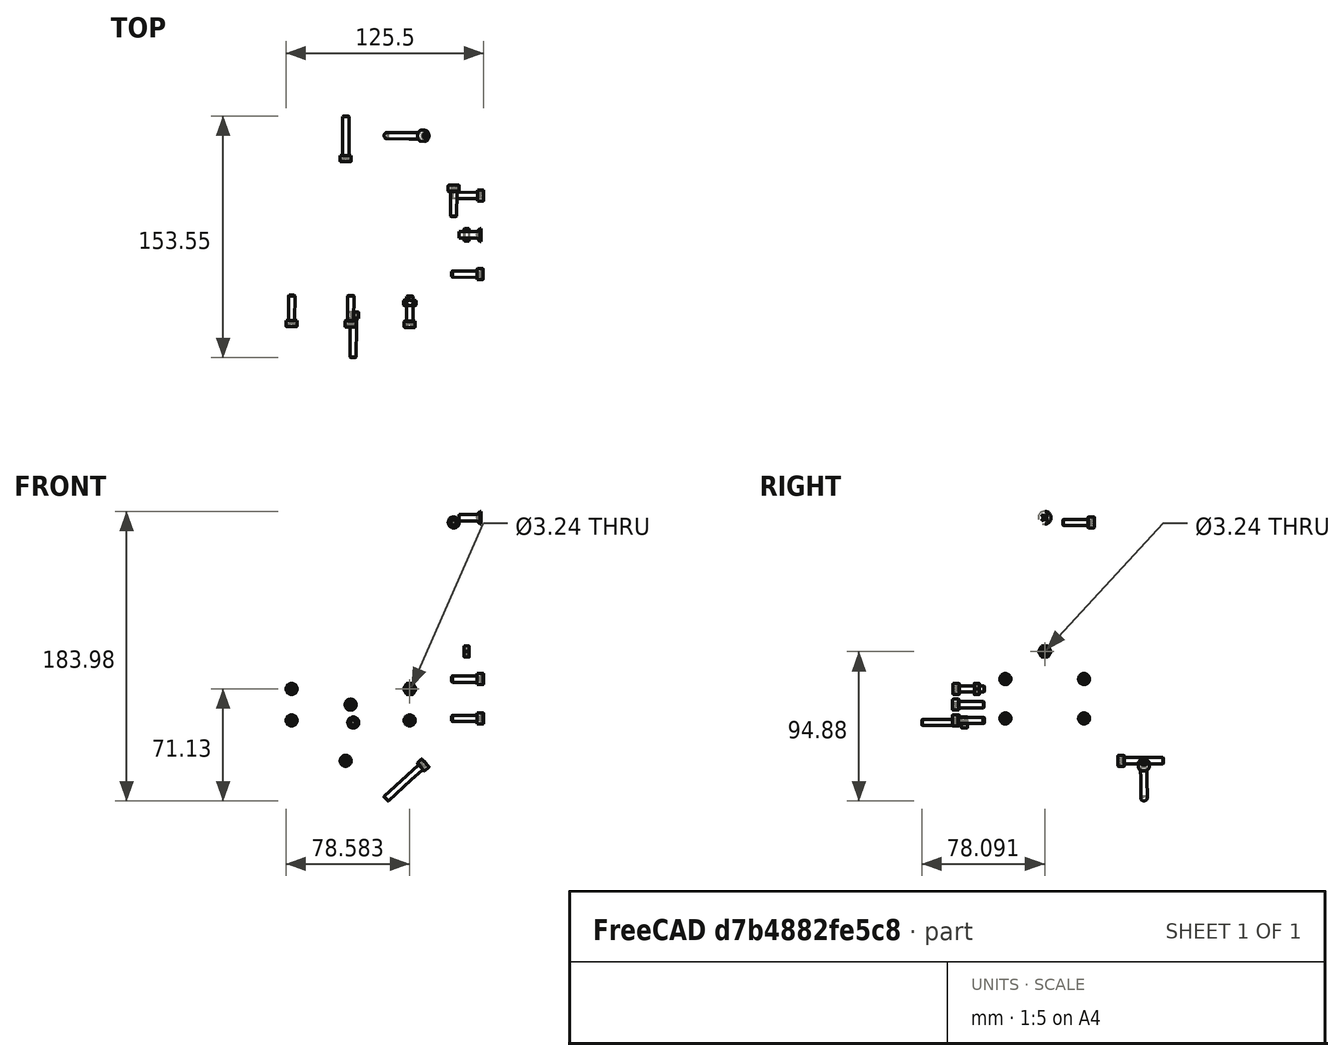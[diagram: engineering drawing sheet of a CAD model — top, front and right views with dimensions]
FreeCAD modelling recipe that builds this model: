
FCSTD DOCUMENT  (FreeCAD 1.1R42987 (Git))
Label: RobotAssembly
License: All rights reserved
LicenseURL: https://en.wikipedia.org/wiki/All_rights_reserved
objects: App::FeaturePython×68, App::Link×52, Part::FeaturePython×15, App::Point×3, Assembly::JointGroup×3, Assembly::AssemblyObject×3
note: 15 computed .brp shape members not serialized (recipe doc carries the construction recipe); baked Part::Feature solids carry a one-line shape summary decoded from their .brp
EXTERNAL_REF file=Body/Body.FCStd obj=Body
EXTERNAL_REF file=Imports/Neverest 20 Orbital.FCStd obj=am_3637_NeveRest_Orbital_20_Gearmotor_REV2
EXTERNAL_REF file=Body/Body.FCStd obj=Body001
EXTERNAL_REF file=Body/Body.FCStd obj=Body002
EXTERNAL_REF file=Imports/RaspberryPi3B+.FCStd obj=Ras_Pi_3B_
EXTERNAL_REF file=Body/Body.FCStd obj=Body003
EXTERNAL_REF file=Imports/MISUMI-Sar220.FCStd obj=Part__Feature001
EXTERNAL_REF file=Imports/V-Groove.FCStd obj=_609_0613_0004
EXTERNAL_REF file=Imports/V-Groove.FCStd obj=Body
EXTERNAL_REF file=Wheel/Wheel.FCStd obj=Body
EXTERNAL_REF file=Wheel/Wheel.FCStd obj=Body001
EXTERNAL_REF file=Slides Plate/SlidesPlate.FCStd obj=Body
EXTERNAL_REF file=Imports/MISUMI-Sar220.FCStd obj=Part__Feature
EXTERNAL_REF file=Variables.FCStd obj=Spreadsheet
EXTERNAL_REF file=Body/Body.FCStd obj=Body004
EXTERNAL_REF file=Body/Body.FCStd obj=Body007
EXTERNAL_REF file=Imports/Fan.FCStd obj=GUNCAIZHU_Ventilator_30x30x7_5_5V
EXTERNAL_REF file=Slides Motor Mount/SlidesMotorMount.FCStd obj=Body
EXTERNAL_REF file=Spool/Spool.FCStd obj=Body
EXTERNAL_REF file=Spool/Spool.FCStd obj=Body001
EXTERNAL_REF file=Passive Claw/PassiveClaw.FCStd obj=Part__Mirroring
EXTERNAL_REF file=Passive Claw/PassiveClaw.FCStd obj=Body
EXTERNAL_REF file=Body/Body.FCStd obj=Body008
EXTERNAL_REF file=Body/Body.FCStd obj=Body009

FEATURE [App::Point] Origin001
  Role = Origin
FEATURE [App::Link] Body
  LinkPlacement = pos=(-23.8017,-14.6889,-3.00006) rot=(0,0,-1;0.005858rad)
  LinkedObject = -> <external Body/Body.FCStd>#Body
  Placement = pos=(-23.8017,-14.6889,-3.00006) rot=(0,0,-1;0.005858rad)
FEATURE [App::Link] am_3637_NeveRest_Orbital_20_Gearmotor_REV2  label="am-3637 NeveRest Orbital 20 Gearmotor REV2"
  LinkPlacement = pos=(-23.0758,-34.8754,-19.558) rot=(0.999991,-0.002929,-0.002929;1.57081rad)
  LinkedObject = -> <external Imports/Neverest 20 Orbital.FCStd>#am_3637_NeveRest_Orbital_20_Gearmotor_REV2
  Placement = pos=(-23.0758,-34.8754,-19.558) rot=(0.999991,-0.002929,-0.002929;1.57081rad)
FEATURE [App::Link] Motor_Mount_Right  label="Motor Mount Right"
  LinkPlacement = pos=(-23.8017,-14.6889,-3.00006) rot=(0,0,-1;0.005858rad)
  LinkedObject = -> <external Body/Body.FCStd>#Body001
  Placement = pos=(-23.8017,-14.6889,-3.00006) rot=(0,0,-1;0.005858rad)
FEATURE [App::Link] Link  label="am-3637 NeveRest Orbital 20 Gearmotor REV003"
  LinkPlacement = pos=(-24.5276,5.49757,-19.558) rot=(0.002071,0.707105,0.707105;3.13745rad)
  LinkedObject = -> am_3637_NeveRest_Orbital_20_Gearmotor_REV2
  Placement = pos=(-24.5276,5.49757,-19.558) rot=(0.002071,0.707105,0.707105;3.13745rad)
FEATURE [App::Link] Slides_Mount  label="Slides Mount"
  LinkPlacement = pos=(-23.8017,-14.6889,-3.00006) rot=(0,0,-1;0.005858rad)
  LinkedObject = -> <external Body/Body.FCStd>#Body002
  Placement = pos=(-23.8017,-14.6889,-3.00006) rot=(0,0,-1;0.005858rad)
FEATURE [App::FeaturePython] Joint009  label="Fixed005"  # Assembly joint (typed FeaturePython)
  AngleMax = 0
  AngleMin = 0
  Detach1 = false
  Detach2 = false
  Distance = 0
  Distance2 = 0
  EnableAngleMax = false
  EnableAngleMin = false
  EnableLengthMax = false
  EnableLengthMin = false
  JointType = 0 (Fixed)
  LengthMax = 0
  LengthMin = 0
  Placement1 = pos=(75,25,30) rot=(0.57735,0.57735,0.57735;2.0944rad)
  Placement2 = pos=(75,25,30) rot=(0.57735,0.57735,0.57735;2.0944rad)
  Reference1 = -> Assembly [Slides_Mount.Edge32,Slides_Mount.Edge32]
  Reference2 = -> Assembly [Body.Edge44,Body.Edge44]
  Suppressed = false
FEATURE [Part::FeaturePython] Screw  label="M4x16-Screw124"  # WARN: FeaturePython — macro-defined, semantics opaque (R4)
  Diameter = 5
  Invert = false
  LeftHanded = false
  Length = 5
  LengthCustom = 16
  MatchOuter = false
  OffsetAngle = 0
  Placement = pos=(56.0505,-40.1572,26.9999) rot=(0.579605,0.576219,0.576219;2.09102rad)
  Thread = false
  Type = 74
FEATURE [App::FeaturePython] Joint012  label="Fixed007"  # Assembly joint (typed FeaturePython)
  AngleMax = 0
  AngleMin = 0
  Detach1 = false
  Detach2 = false
  Distance = 0
  Distance2 = 0
  EnableAngleMax = false
  EnableAngleMin = false
  EnableLengthMax = false
  EnableLengthMin = false
  JointType = 0 (Fixed)
  LengthMax = 0
  LengthMin = 0
  Placement2 = pos=(80,-25,30) rot=(0.57735,0.57735,0.57735;2.0944rad)
  Reference1 = -> Assembly [Screw.Edge26,Screw.Edge26]
  Reference2 = -> Assembly [Slides_Mount.Edge53,Slides_Mount.Edge53]
  Suppressed = false
FEATURE [Part::FeaturePython] Screw001  label="M4x16-Screw"  # WARN: FeaturePython — macro-defined, semantics opaque (R4)
  Diameter = 5
  Invert = false
  LeftHanded = false
  Length = 5
  LengthCustom = 16
  MatchOuter = false
  OffsetAngle = 0
  Placement = pos=(56.3434,9.84197,26.9999) rot=(0.579605,0.576219,0.576219;2.09102rad)
  Thread = false
  Type = 74
  expr: LengthCustom = <<M4x16-Screw124>>.LengthCustom
FEATURE [Part::FeaturePython] Screw002  label="M4x16-Screw125"  # WARN: FeaturePython — macro-defined, semantics opaque (R4)
  Diameter = 5
  Invert = false
  LeftHanded = false
  Length = 5
  LengthCustom = 16
  MatchOuter = false
  OffsetAngle = 0
  Placement = pos=(56.0505,-40.1572,1.99994) rot=(0.579605,0.576219,0.576219;2.09102rad)
  Thread = false
  Type = 74
  expr: LengthCustom = <<M4x16-Screw124>>.LengthCustom
FEATURE [Part::FeaturePython] Screw003  label="M4x16-Screw126"  # WARN: FeaturePython — macro-defined, semantics opaque (R4)
  Diameter = 5
  Invert = false
  LeftHanded = false
  Length = 5
  LengthCustom = 16
  MatchOuter = false
  OffsetAngle = 0
  Placement = pos=(56.3434,9.84197,1.99994) rot=(0.579605,0.576219,0.576219;2.09102rad)
  Thread = false
  Type = 74
  expr: LengthCustom = <<M4x16-Screw124>>.LengthCustom
FEATURE [App::FeaturePython] Joint013  label="Fixed008"  # Assembly joint (typed FeaturePython)
  AngleMax = 0
  AngleMin = 0
  Detach1 = false
  Detach2 = false
  Distance = 0
  Distance2 = 0
  EnableAngleMax = false
  EnableAngleMin = false
  EnableLengthMax = false
  EnableLengthMin = false
  JointType = 0 (Fixed)
  LengthMax = 0
  LengthMin = 0
  Placement2 = pos=(80,-25,5) rot=(0.57735,0.57735,0.57735;2.0944rad)
  Reference1 = -> Assembly [Screw002.Edge26,Screw002.Edge26]
  Reference2 = -> Assembly [Slides_Mount.Edge52,Slides_Mount.Edge52]
  Suppressed = false
FEATURE [App::FeaturePython] Joint014  label="Fixed009"  # Assembly joint (typed FeaturePython)
  AngleMax = 0
  AngleMin = 0
  Detach1 = false
  Detach2 = false
  Distance = 0
  Distance2 = 0
  EnableAngleMax = false
  EnableAngleMin = false
  EnableLengthMax = false
  EnableLengthMin = false
  JointType = 0 (Fixed)
  LengthMax = 0
  LengthMin = 0
  Placement2 = pos=(80,25,30) rot=(0.57735,0.57735,0.57735;2.0944rad)
  Reference1 = -> Assembly [Screw001.Edge26,Screw001.Edge26]
  Reference2 = -> Assembly [Slides_Mount.Edge51,Slides_Mount.Edge51]
  Suppressed = false
FEATURE [App::FeaturePython] Joint015  label="Fixed010"  # Assembly joint (typed FeaturePython)
  AngleMax = 0
  AngleMin = 0
  Detach1 = false
  Detach2 = false
  Distance = 0
  Distance2 = 0
  EnableAngleMax = false
  EnableAngleMin = false
  EnableLengthMax = false
  EnableLengthMin = false
  JointType = 0 (Fixed)
  LengthMax = 0
  LengthMin = 0
  Placement2 = pos=(80,25,5) rot=(0.57735,0.57735,0.57735;2.0944rad)
  Reference1 = -> Assembly [Screw003.Edge26,Screw003.Edge26]
  Reference2 = -> Assembly [Slides_Mount.Edge50,Slides_Mount.Edge50]
  Suppressed = false
FEATURE [Part::FeaturePython] Screw004  label="M4x16-Screw127"  # WARN: FeaturePython — macro-defined, semantics opaque (R4)
  Diameter = 5
  Invert = false
  LeftHanded = false
  Length = 5
  LengthCustom = 16
  MatchOuter = false
  OffsetAngle = 0
  Placement = pos=(-61.6233,-69.4683,20.7499) rot=(0.999991,-0.002929,-0.002929;1.57081rad)
  Thread = false
  Type = 74
  expr: LengthCustom = <<M4x16-Screw124>>.LengthCustom
FEATURE [Part::FeaturePython] Screw005  label="M4x16-Screw128"  # WARN: FeaturePython — macro-defined, semantics opaque (R4)
  Diameter = 5
  Invert = false
  LeftHanded = false
  Length = 5
  LengthCustom = 16
  MatchOuter = false
  OffsetAngle = 0
  Placement = pos=(-61.6233,-69.4683,0.749943) rot=(0.999991,-0.002929,-0.002929;1.57081rad)
  Thread = false
  Type = 74
  expr: LengthCustom = <<M4x16-Screw127>>.LengthCustom
FEATURE [Part::FeaturePython] Screw006  label="M4x16-Screw129"  # WARN: FeaturePython — macro-defined, semantics opaque (R4)
  Diameter = 5
  Invert = false
  LeftHanded = false
  Length = 5
  LengthCustom = 16
  MatchOuter = false
  OffsetAngle = 0
  Placement = pos=(-24.1239,-69.688,10.7499) rot=(0.999991,-0.002929,-0.002929;1.57081rad)
  Thread = false
  Type = 74
  expr: LengthCustom = <<M4x16-Screw127>>.LengthCustom
FEATURE [Part::FeaturePython] Screw007  label="M4x16-Screw130"  # WARN: FeaturePython — macro-defined, semantics opaque (R4)
  Diameter = 5
  Invert = false
  LeftHanded = false
  Length = 5
  LengthCustom = 16
  MatchOuter = false
  OffsetAngle = 0
  Placement = pos=(13.3754,-69.9077,0.749943) rot=(0.999991,-0.002929,-0.002929;1.57081rad)
  Thread = false
  Type = 74
  expr: LengthCustom = <<M4x16-Screw127>>.LengthCustom
FEATURE [App::Link] Link001  label="M4x16-Screw026"
  LinkPlacement = pos=(13.3754,-69.9077,20.7499) rot=(0.999991,-0.002929,-0.002929;1.57081rad)
  LinkedObject = -> Screw007
  Placement = pos=(13.3754,-69.9077,20.7499) rot=(0.999991,-0.002929,-0.002929;1.57081rad)
FEATURE [App::Link] Ras_Pi_3B_179  label="Ras Pi 3B+179"
  LinkPlacement = pos=(-12.1701,7.74332,-5.72205e-05) rot=(0.002071,0.707105,0.707105;3.13745rad)
  LinkedObject = -> <external Imports/RaspberryPi3B+.FCStd>#Ras_Pi_3B_
  Placement = pos=(-12.1701,7.74332,-5.72205e-05) rot=(0.002071,0.707105,0.707105;3.13745rad)
FEATURE [Part::FeaturePython] Screw008  label="M4x14-Screw"  # WARN: FeaturePython — macro-defined, semantics opaque (R4)
  Diameter = 6
  Invert = false
  LeftHanded = false
  Length = 4
  LengthCustom = 14
  MatchOuter = false
  OffsetAngle = 0
  Placement = pos=(58.7504,-15.1726,129.5) rot=(0.002929,0.999991,-0.002929;1.57081rad)
  Thread = false
  Type = 77
FEATURE [App::Link] Link002  label="M4x14-Screw001"
  LinkPlacement = pos=(58.7504,-15.1726,44.4999) rot=(0.002929,0.999991,-0.002929;1.57081rad)
  LinkedObject = -> Screw008
  Placement = pos=(58.7504,-15.1726,44.4999) rot=(0.002929,0.999991,-0.002929;1.57081rad)
FEATURE [Part::FeaturePython] Nut  label="M4-Nut"  # WARN: FeaturePython — macro-defined, semantics opaque (R4)
  Diameter = 6
  Invert = false
  LeftHanded = false
  MatchOuter = false
  OffsetAngle = 0
  Placement = pos=(47.9971,-15.1096,44.4999) rot=(0.579605,0.576219,0.576219;2.09102rad)
  Thread = false
  Type = 31
FEATURE [App::FeaturePython] Joint023  label="Fixed017"  # Assembly joint (typed FeaturePython)
  AngleMax = 0
  AngleMin = 0
  Detach1 = false
  Detach2 = false
  Distance = 0
  Distance2 = 0
  EnableAngleMax = false
  EnableAngleMin = false
  EnableLengthMax = false
  EnableLengthMin = false
  JointType = 0 (Fixed)
  LengthMax = 0
  LengthMin = 0
  Placement1 = pos=(0,0,3.2) rot=(0,0,1;0rad)
  Placement2 = pos=(75,-5.86e-14,47.5) rot=(0.57735,0.57735,0.57735;2.0944rad)
  Reference1 = -> Assembly [Nut.Edge2,Nut.Edge2]
  Reference2 = -> Assembly [Slides_Mount.Edge34,Slides_Mount.Edge34]
  Suppressed = false
FEATURE [App::FeaturePython] Joint027  label="Fixed021"  # Assembly joint (typed FeaturePython)
  AngleMax = 0
  AngleMin = 0
  Detach1 = false
  Detach2 = false
  Distance = 0
  Distance2 = 0
  EnableAngleMax = false
  EnableAngleMin = false
  EnableLengthMax = false
  EnableLengthMin = false
  JointType = 0 (Fixed)
  LengthMax = 0
  LengthMin = 0
  Offset2 = pos=(0,0,0) rot=(0,0,1;1.5708rad)
  Placement1 = pos=(-50,-30,3) rot=(0,0,1;0rad)
  Placement2 = pos=(61.5,0,-52.5) rot=(0,0.707107,0.707107;3.14159rad)
  Reference1 = -> Assembly [Body.Edge214,Body.Edge214]
  Reference2 = -> Assembly [Ras_Pi_3B_179.Part__Feature014.Edge10,Ras_Pi_3B_179.Part__Feature014.Edge10]
  Suppressed = false
FEATURE [App::Link] Body_Top  label="Body Top"
  LinkPlacement = pos=(-23.8017,-14.6889,-3.00006) rot=(0,0,-1;0.005858rad)
  LinkedObject = -> <external Body/Body.FCStd>#Body003
  Placement = pos=(-23.8017,-14.6889,-3.00006) rot=(0,0,-1;0.005858rad)
FEATURE [App::FeaturePython] Joint028  label="Fixed022"  # Assembly joint (typed FeaturePython)
  AngleMax = 0
  AngleMin = 0
  Detach1 = false
  Detach2 = false
  Distance = 0
  Distance2 = 0
  EnableAngleMax = false
  EnableAngleMin = false
  EnableLengthMax = false
  EnableLengthMin = false
  JointType = 0 (Fixed)
  LengthMax = 0
  LengthMin = 0
  Placement1 = pos=(-66,-41,35) rot=(0,0,1;0rad)
  Placement2 = pos=(-66,-41,35) rot=(0,0,1;0rad)
  Reference1 = -> Assembly [Body.Edge21,Body.Edge21]
  Reference2 = -> Assembly [Body_Top.Edge98,Body_Top.Edge98]
  Suppressed = false
FEATURE [Part::FeaturePython] Nut001  label="M4-Nut014"  # WARN: FeaturePython — macro-defined, semantics opaque (R4)
  Diameter = 6
  Invert = false
  LeftHanded = false
  MatchOuter = false
  OffsetAngle = 0
  Placement = pos=(13.4528,-56.7079,20.7499) rot=(0.999991,-0.002929,-0.002929;1.57081rad)
  Thread = false
  Type = 31
FEATURE [App::FeaturePython] Joint029  label="Fixed023"  # Assembly joint (typed FeaturePython)
  AngleMax = 0
  AngleMin = 0
  Detach1 = false
  Detach2 = false
  Distance = 0
  Distance2 = 0
  EnableAngleMax = false
  EnableAngleMin = false
  EnableLengthMax = false
  EnableLengthMin = false
  JointType = 0 (Fixed)
  LengthMax = 0
  LengthMin = 0
  Placement1 = pos=(0,-3.6e-15,3.2) rot=(0,0,1;0rad)
  Placement2 = pos=(37.5,-45,23.75) rot=(1,0,0;1.5708rad)
  Reference1 = -> Assembly [Nut001.Edge2,Nut001.Edge2]
  Reference2 = -> Assembly [Body.Edge89,Body.Edge89]
  Suppressed = false
FEATURE [App::Link] Link004  label="M4-Nut003"
  LinkPlacement = pos=(-23.5193,33.5103,10.7499) rot=(0.999991,-0.002929,-0.002929;1.57081rad)
  LinkedObject = -> Nut001
  Placement = pos=(-23.5193,33.5103,10.7499) rot=(0.999991,-0.002929,-0.002929;1.57081rad)
FEATURE [App::Link] Link005  label="M4-Nut004"
  LinkPlacement = pos=(-61.0562,27.3301,0.749943) rot=(0.999991,-0.002929,0.002929;4.71238rad)
  LinkedObject = -> Link004
  Placement = pos=(-61.0562,27.3301,0.749943) rot=(0.999991,-0.002929,0.002929;4.71238rad)
FEATURE [App::Link] Link007  label="M4-Nut006"
  LinkPlacement = pos=(-61.5459,-56.2685,20.7499) rot=(0.999991,-0.002929,-0.002929;1.57081rad)
  LinkedObject = -> Nut
  Placement = pos=(-61.5459,-56.2685,20.7499) rot=(0.999991,-0.002929,-0.002929;1.57081rad)
FEATURE [App::Link] Link008  label="M4-Nut007"
  LinkPlacement = pos=(13.9613,30.0906,0.749943) rot=(-0.002071,-0.707105,0.707105;3.13745rad)
  LinkedObject = -> Link007
  Placement = pos=(13.9613,30.0906,0.749943) rot=(-0.002071,-0.707105,0.707105;3.13745rad)
FEATURE [App::Link] Link009  label="M4-Nut008"
  LinkPlacement = pos=(-61.0562,27.3301,20.7499) rot=(0.999991,-0.002929,0.002929;4.71238rad)
  LinkedObject = -> Link008
  Placement = pos=(-61.0562,27.3301,20.7499) rot=(0.999991,-0.002929,0.002929;4.71238rad)
FEATURE [App::Link] Link010  label="M4-Nut009"
  LinkPlacement = pos=(42.8507,-40.0798,26.9999) rot=(0.579605,0.576219,0.576219;2.09102rad)
  LinkedObject = -> Link009
  Placement = pos=(42.8507,-40.0798,26.9999) rot=(0.579605,0.576219,0.576219;2.09102rad)
FEATURE [App::FeaturePython] Joint031  label="Fixed025"  # Assembly joint (typed FeaturePython)
  AngleMax = 0
  AngleMin = 0
  Detach1 = false
  Detach2 = false
  Distance = 0
  Distance2 = 0
  EnableAngleMax = false
  EnableAngleMin = false
  EnableLengthMax = false
  EnableLengthMin = false
  JointType = 0 (Fixed)
  LengthMax = 0
  LengthMin = 0
  Placement1 = pos=(0,-3.6e-15,3.2) rot=(0,0,1;0rad)
  Placement2 = pos=(-37.5,-45,23.75) rot=(1,0,0;1.5708rad)
  Reference1 = -> Assembly [Link007.Edge2,Link007.Edge2]
  Reference2 = -> Assembly [Body.Edge88,Body.Edge88]
  Suppressed = false
FEATURE [App::FeaturePython] Joint034  label="Fixed028"  # Assembly joint (typed FeaturePython)
  AngleMax = 0
  AngleMin = 0
  Detach1 = false
  Detach2 = false
  Distance = 0
  Distance2 = 0
  EnableAngleMax = false
  EnableAngleMin = false
  EnableLengthMax = false
  EnableLengthMin = false
  JointType = 0 (Fixed)
  LengthMax = 0
  LengthMin = 0
  Placement1 = pos=(7.1e-15,0,3.2) rot=(0,0,1;0rad)
  Placement2 = pos=(-37.5,45,23.75) rot=(1,0,0;1.5708rad)
  Reference1 = -> Assembly [Link009.Edge2,Link009.Edge2]
  Reference2 = -> Assembly [Body.Edge122,Body.Edge122]
  Suppressed = false
FEATURE [App::Link] Link011  label="M4-Nut010"
  LinkPlacement = pos=(13.9425,26.8907,20.7499) rot=(0.999991,-0.002929,0.002929;4.71238rad)
  LinkedObject = -> Link009
  Placement = pos=(13.9425,26.8907,20.7499) rot=(0.999991,-0.002929,0.002929;4.71238rad)
FEATURE [App::Link] Link012  label="M4-Nut011"
  LinkPlacement = pos=(43.1436,9.9193,1.99994) rot=(0.579605,0.576219,0.576219;2.09102rad)
  LinkedObject = -> Link008
  Placement = pos=(43.1436,9.9193,1.99994) rot=(0.579605,0.576219,0.576219;2.09102rad)
FEATURE [App::Link] Link013  label="M4-Nut012"
  LinkPlacement = pos=(43.1436,9.9193,26.9999) rot=(0.579605,0.576219,0.576219;2.09102rad)
  LinkedObject = -> Link010
  Placement = pos=(43.1436,9.9193,26.9999) rot=(0.579605,0.576219,0.576219;2.09102rad)
FEATURE [App::FeaturePython] Joint037  label="Fixed031"  # Assembly joint (typed FeaturePython)
  AngleMax = 0
  AngleMin = 0
  Detach1 = false
  Detach2 = false
  Distance = 0
  Distance2 = 0
  EnableAngleMax = false
  EnableAngleMin = false
  EnableLengthMax = false
  EnableLengthMin = false
  JointType = 0 (Fixed)
  LengthMax = 0
  LengthMin = 0
  Placement1 = pos=(0,0,3.2) rot=(0,0,1;0rad)
  Placement2 = pos=(37.5,45,23.75) rot=(1,0,0;1.5708rad)
  Reference1 = -> Assembly [Link011.Edge2,Link011.Edge2]
  Reference2 = -> Assembly [Body.Edge121,Body.Edge121]
  Suppressed = false
FEATURE [App::Link] Link014  label="M4x16-Screw034"
  LinkPlacement = pos=(-23.4795,40.3101,10.7499) rot=(0.002071,0.707105,0.707105;3.13745rad)
  LinkedObject = -> Screw004
  Placement = pos=(-23.4795,40.3101,10.7499) rot=(0.002071,0.707105,0.707105;3.13745rad)
FEATURE [App::Link] Link015  label="M4x16-Screw035"
  LinkPlacement = pos=(-60.9788,40.5298,20.7499) rot=(0.002071,0.707105,0.707105;3.13745rad)
  LinkedObject = -> Link014
  Placement = pos=(-60.9788,40.5298,20.7499) rot=(0.002071,0.707105,0.707105;3.13745rad)
FEATURE [App::Link] Link016  label="M4x16-Screw036"
  LinkPlacement = pos=(14.0199,40.0904,0.749943) rot=(0.002071,0.707105,0.707105;3.13745rad)
  LinkedObject = -> Link015
  Placement = pos=(14.0199,40.0904,0.749943) rot=(0.002071,0.707105,0.707105;3.13745rad)
FEATURE [App::Link] Link017  label="M4x16-Screw037"
  LinkPlacement = pos=(-60.9788,40.5298,0.749943) rot=(0.002071,0.707105,0.707105;3.13745rad)
  LinkedObject = -> Link016
  Placement = pos=(-60.9788,40.5298,0.749943) rot=(0.002071,0.707105,0.707105;3.13745rad)
FEATURE [App::Link] Link018  label="M4x16-Screw038"
  LinkPlacement = pos=(14.0199,40.0904,20.7499) rot=(0.002071,0.707105,0.707105;3.13745rad)
  LinkedObject = -> Link017
  Placement = pos=(14.0199,40.0904,20.7499) rot=(0.002071,0.707105,0.707105;3.13745rad)
FEATURE [App::FeaturePython] GroundedJoint  # Assembly grounded joint (typed FeaturePython)
  ObjectToGround = -> Body
FEATURE [App::Link] SAR2_20_b  label="SAR2-20_b"
  LinkPlacement = pos=(63.5382,-25.2008,-55.5001) rot=(0,0,-1;0.005858rad)
  LinkedObject = -> <external Imports/MISUMI-Sar220.FCStd>#Part__Feature001
  Placement = pos=(63.5382,-25.2008,-55.5001) rot=(0,0,-1;0.005858rad)
FEATURE [App::FeaturePython] Joint045  label="Fixed038"  # Assembly joint (typed FeaturePython)
  AngleMax = 0
  AngleMin = 0
  Detach1 = false
  Detach2 = false
  Distance = 0
  Distance2 = 0
  EnableAngleMax = false
  EnableAngleMin = false
  EnableLengthMax = false
  EnableLengthMin = false
  JointType = 0 (Fixed)
  LengthMax = 0
  LengthMin = 0
  Offset2 = pos=(0,0,0) rot=(0,0,-1;1.5708rad)
  Placement1 = pos=(-7.4,10,185) rot=(0,1,0;1.5708rad)
  Placement2 = pos=(80,-5.68e-14,132.5) rot=(0,1,0;1.5708rad)
  Reference1 = -> Assembly [SAR2_20_b.Edge129,SAR2_20_b.Edge129]
  Reference2 = -> Assembly [Slides_Mount.Edge48,Slides_Mount.Edge48]
  Suppressed = false
FEATURE [App::FeaturePython] Joint046  label="Fixed039"  # Assembly joint (typed FeaturePython)
  AngleMax = 0
  AngleMin = 0
  Detach1 = false
  Detach2 = false
  Distance = 0
  Distance2 = 0
  EnableAngleMax = false
  EnableAngleMin = false
  EnableLengthMax = false
  EnableLengthMin = false
  JointType = 0 (Fixed)
  LengthMax = 0
  LengthMin = 0
  Placement1 = pos=(0,1.8e-15,-2.55355) rot=(0,0,1;0rad)
  Placement2 = pos=(-7.4,10,185) rot=(0,1,0;1.5708rad)
  Reference1 = -> Assembly [Screw008.Edge4,Screw008.Edge4]
  Reference2 = -> Assembly [SAR2_20_b.Edge129,SAR2_20_b.Edge129]
  Suppressed = false
FEATURE [App::FeaturePython] Joint047  label="Fixed040"  # Assembly joint (typed FeaturePython)
  AngleMax = 0
  AngleMin = 0
  Detach1 = false
  Detach2 = false
  Distance = 0
  Distance2 = 0
  EnableAngleMax = false
  EnableAngleMin = false
  EnableLengthMax = false
  EnableLengthMin = false
  JointType = 0 (Fixed)
  LengthMax = 0
  LengthMin = 0
  Placement1 = pos=(0,1.8e-15,-2.55355) rot=(0,0,1;0rad)
  Placement2 = pos=(-7.4,10,100) rot=(0,1,0;1.5708rad)
  Reference1 = -> Assembly [Link002.Edge4,Link002.Edge4]
  Reference2 = -> Assembly [SAR2_20_b.Edge130,SAR2_20_b.Edge130]
  Suppressed = false
FEATURE [App::Link] _609_0613_0007  label="1609-0613-0007"
  LinkPlacement = pos=(41.3026,2.92997,126.5) rot=(0.002929,0.999991,-0.002929;1.57081rad)
  LinkedObject = -> <external Imports/V-Groove.FCStd>#_609_0613_0004
  Placement = pos=(41.3026,2.92997,126.5) rot=(0.002929,0.999991,-0.002929;1.57081rad)
FEATURE [App::Link] StringGuard
  LinkPlacement = pos=(41.3041,3.17997,126.5) rot=(0,0,-1;0.005858rad)
  LinkedObject = -> <external Imports/V-Groove.FCStd>#Body
  Placement = pos=(41.3041,3.17997,126.5) rot=(0,0,-1;0.005858rad)
FEATURE [Part::FeaturePython] Screw009  label="M4x16-Screw131"  # WARN: FeaturePython — macro-defined, semantics opaque (R4)
  Diameter = 5
  Invert = false
  LeftHanded = false
  Length = 11
  LengthCustom = 16
  MatchOuter = false
  OffsetAngle = 0
  Placement = pos=(41.3583,12.4298,126.5) rot=(0.999991,-0.002929,0.002929;4.71238rad)
  Thread = false
  Type = 74
  expr: LengthCustom = <<M4x16-Screw124>>.LengthCustom
FEATURE [App::FeaturePython] Joint053  label="Fixed045"  # Assembly joint (typed FeaturePython)
  AngleMax = 0
  AngleMin = 0
  Detach1 = false
  Detach2 = false
  Distance = 0
  Distance2 = 0
  EnableAngleMax = false
  EnableAngleMin = false
  EnableLengthMax = false
  EnableLengthMin = false
  JointType = 0 (Fixed)
  LengthMax = 0
  LengthMin = 0
  Offset2 = pos=(0,0,0) rot=(0,0,1;3.14159rad)
  Placement1 = pos=(-7.1e-15,-3.25,0) rot=(1,0,0;1.5708rad)
  Placement2 = pos=(65,15,129.5) rot=(1,0,0;4.71239rad)
  Reference1 = -> Assembly [StringGuard.Edge9,StringGuard.Edge9]
  Reference2 = -> Assembly [Slides_Mount.Edge58,Slides_Mount.Edge58]
  Suppressed = false
FEATURE [App::FeaturePython] Joint054  label="Fixed046"  # Assembly joint (typed FeaturePython)
  AngleMax = 0
  AngleMin = 0
  Detach1 = false
  Detach2 = false
  Distance = 0
  Distance2 = 0
  EnableAngleMax = false
  EnableAngleMin = false
  EnableLengthMax = false
  EnableLengthMin = false
  JointType = 0 (Fixed)
  LengthMax = 0
  LengthMin = 0
  Placement1 = pos=(-7.1e-15,9.25,0) rot=(1,0,0;1.5708rad)
  Reference1 = -> Assembly [StringGuard.Edge35,StringGuard.Edge35]
  Reference2 = -> Assembly [Screw009.Edge26,Screw009.Edge26]
  Suppressed = false
FEATURE [App::FeaturePython] Joint055  label="Revolute047"  # Assembly joint (typed FeaturePython)
  AngleMax = 0
  AngleMin = 0
  Detach1 = false
  Detach2 = false
  Distance = 0
  Distance2 = 0
  EnableAngleMax = false
  EnableAngleMin = false
  EnableLengthMax = false
  EnableLengthMin = false
  JointType = 1 (Revolute)
  LengthMax = 0
  LengthMin = 0
  Placement1 = pos=(0,0,0) rot=(0.57735,-0.57735,0.57735;2.0944rad)
  Placement2 = pos=(-7.1e-15,-0.25,0) rot=(1,0,0;1.5708rad)
  Reference1 = -> Assembly [_609_0613_0007.Part__Feature002.Edge108,_609_0613_0007.Part__Feature002.Edge108]
  Reference2 = -> Assembly [StringGuard.Edge2,StringGuard.Edge2]
  Suppressed = false
FEATURE [App::Link] Link020  label="Motor Mount Right001"
  LinkPlacement = pos=(-23.8017,-14.6889,-3.00006) rot=(0,0,1;3.13573rad)
  LinkedObject = -> Motor_Mount_Right
  Placement = pos=(-23.8017,-14.6889,-3.00006) rot=(0,0,1;3.13573rad)
FEATURE [App::FeaturePython] Joint056  label="Fixed048"  # Assembly joint (typed FeaturePython)
  AngleMax = 0
  AngleMin = 0
  Detach1 = false
  Detach2 = false
  Distance = 0
  Distance2 = 0
  EnableAngleMax = false
  EnableAngleMin = false
  EnableLengthMax = false
  EnableLengthMin = false
  JointType = 0 (Fixed)
  LengthMax = 0
  LengthMin = 0
  Placement1 = pos=(-28,-50,-29) rot=(1,0,0;1.5708rad)
  Placement2 = pos=(0,0,32.1564) rot=(0,0,1;0rad)
  Reference1 = -> Assembly [Link020.Edge28,Link020.Edge28]
  Reference2 = -> Assembly [Link.Part__Feature.Edge165,Link.Part__Feature.Edge165]
  Suppressed = false
FEATURE [App::Link] Wheel
  LinkPlacement = pos=(4.66789,64.8507,-31.9659) rot=(-0.29634,0.676219,-0.674471;3.72505rad)
  LinkedObject = -> <external Wheel/Wheel.FCStd>#Body
  Placement = pos=(4.66789,64.8507,-31.9659) rot=(-0.29634,0.676219,-0.674471;3.72505rad)
FEATURE [App::Link] Clamp
  LinkPlacement = pos=(4.66789,64.8507,-31.9659) rot=(-0.29634,0.676219,-0.674471;3.72505rad)
  LinkedObject = -> <external Wheel/Wheel.FCStd>#Body001
  Placement = pos=(4.66789,64.8507,-31.9659) rot=(-0.29634,0.676219,-0.674471;3.72505rad)
FEATURE [App::Link] Link021  label="Clamp001"
  LinkPlacement = pos=(-52.0438,-60.2292,-31.9979) rot=(-0.543151,0.595306,-0.592114;4.1421rad)
  LinkedObject = -> Clamp
  Placement = pos=(-52.0438,-60.2292,-31.9979) rot=(-0.543151,0.595306,-0.592114;4.1421rad)
FEATURE [App::Link] Link022  label="Wheel001"
  LinkPlacement = pos=(-52.241,-94.2287,-32.021) rot=(-0.60929,0.562485,0.558906;2.04236rad)
  LinkedObject = -> Wheel
  Placement = pos=(-52.241,-94.2287,-32.021) rot=(-0.60929,0.562485,0.558906;2.04236rad)
FEATURE [App::Link] Slides_Plate  label="Slides Plate"
  LinkPlacement = pos=(69.1967,-15.2338,-40.5001) rot=(-0.575095,0.578474,0.578474;4.18541rad)
  LinkedObject = -> <external Slides Plate/SlidesPlate.FCStd>#Body
  Placement = pos=(69.1967,-15.2338,-40.5001) rot=(-0.575095,0.578474,0.578474;4.18541rad)
FEATURE [App::Link] SAR2_20_r  label="SAR2-20_r"
  LinkPlacement = pos=(58.3615,-21.2204,-55.5001) rot=(0,0,-1;0.005858rad)
  LinkedObject = -> <external Imports/MISUMI-Sar220.FCStd>#Part__Feature
  Placement = pos=(58.3615,-21.2204,-55.5001) rot=(0,0,-1;0.005858rad)
FEATURE [App::FeaturePython] Joint081  label="Slider"  # Assembly joint (typed FeaturePython)
  AngleMax = 0
  AngleMin = 0
  Detach1 = false
  Detach2 = false
  Distance = 0
  Distance2 = 0
  EnableAngleMax = false
  EnableAngleMin = false
  EnableLengthMax = true
  EnableLengthMin = true
  JointType = 3 (Slider)
  LengthMax = 120
  LengthMin = 0
  Offset1 = pos=(2.9952,0,0) rot=(0,0,1;0rad)
  Placement1 = pos=(-1.90256,10,200) rot=(0,0,1;0rad)
  Placement2 = pos=(3.29741,6.05,200) rot=(0,0,1;0rad)
  Reference1 = -> Assembly [SAR2_20_b.Face57,SAR2_20_b.Face57]
  Reference2 = -> Assembly [SAR2_20_r.Face24,SAR2_20_r.Face24]
  Suppressed = false
FEATURE [App::FeaturePython] Joint082  label="Fixed059"  # Assembly joint (typed FeaturePython)
  AngleMax = 0
  AngleMin = 0
  Detach1 = false
  Detach2 = false
  Distance = 0
  Distance2 = 0
  EnableAngleMax = false
  EnableAngleMin = false
  EnableLengthMax = false
  EnableLengthMin = false
  JointType = 0 (Fixed)
  LengthMax = 0
  LengthMin = 0
  Offset2 = pos=(0,0,0) rot=(0,0,-1;1.5708rad)
  Placement1 = pos=(1.8e-15,7.82e-14,5) rot=(0,0,1;0rad)
  Placement2 = pos=(5.8,6.05,15) rot=(-0.57735,0.57735,-0.57735;2.0944rad)
  Reference1 = -> Assembly [Slides_Plate.Edge58,Slides_Plate.Edge58]
  Reference2 = -> Assembly [SAR2_20_r.Edge60,SAR2_20_r.Edge60]
  Suppressed = false
FEATURE [App::Point] Origin003
  Role = Origin
FEATURE [Assembly::JointGroup] Joints001
FEATURE [Assembly::AssemblyObject] Assembly001
  Group = -> [Joints001]
  Origin = -> Origin002
  Type = Assembly
FEATURE [App::FeaturePython] Joint083  label="Revolute065"  # Assembly joint (typed FeaturePython)
  AngleMax = 0
  AngleMin = 0
  Detach1 = false
  Detach2 = false
  Distance = 0
  Distance2 = 0
  EnableAngleMax = false
  EnableAngleMin = false
  EnableLengthMax = false
  EnableLengthMin = false
  JointType = 1 (Revolute)
  LengthMax = 0
  LengthMin = 0
  Offset2 = pos=(0,0,5) rot=(0,0,1;0rad)
  Placement1 = pos=(-0.0231521,0.025307,21.5) rot=(0,0,1;0rad)
  Placement2 = pos=(0,0,40.3614) rot=(0,0,1;0rad)
  Reference1 = -> Assembly [Wheel.Edge52,Wheel.Edge52]
  Reference2 = -> Assembly [Link.Part__Feature.Edge15,Link.Part__Feature.Edge15]
  Suppressed = false
FEATURE [App::FeaturePython] Joint084  label="Fixed061"  # Assembly joint (typed FeaturePython)
  AngleMax = 0
  AngleMin = 0
  Detach1 = false
  Detach2 = false
  Distance = 0
  Distance2 = 0
  EnableAngleMax = false
  EnableAngleMin = false
  EnableLengthMax = false
  EnableLengthMin = false
  JointType = 0 (Fixed)
  LengthMax = 0
  LengthMin = 0
  Offset2 = pos=(0,0,1.5) rot=(0,0,1;0rad)
  Placement1 = pos=(-8.46528,0.75,17) rot=(0,0.707107,0.707107;3.14159rad)
  Placement2 = pos=(-8.46528,0.75,17) rot=(0,0.707107,0.707107;3.14159rad)
  Reference1 = -> Assembly [Clamp.Edge30,Clamp.Edge30]
  Reference2 = -> Assembly [Wheel.Edge31,Wheel.Edge31]
  Suppressed = false
  expr: .Offset2.Base.z = Variables#Spreadsheet.WheelClampToShaftDist
FEATURE [App::FeaturePython] Joint085  label="Revolute064"  # Assembly joint (typed FeaturePython)
  AngleMax = 0
  AngleMin = 0
  Detach1 = false
  Detach2 = false
  Distance = 0
  Distance2 = 0
  EnableAngleMax = false
  EnableAngleMin = false
  EnableLengthMax = false
  EnableLengthMin = false
  JointType = 1 (Revolute)
  LengthMax = 0
  LengthMin = 0
  Offset2 = pos=(0,0,5) rot=(0,0,1;0rad)
  Placement1 = pos=(-0.0231521,0.025307,21.5) rot=(0,0,1;0rad)
  Placement2 = pos=(0,0,40.3614) rot=(0,0,1;0rad)
  Reference1 = -> Assembly [Link022.Edge52,Link022.Edge52]
  Reference2 = -> Assembly [am_3637_NeveRest_Orbital_20_Gearmotor_REV2.Part__Feature.Edge15,am_3637_NeveRest_Orbital_20_Gearmotor_REV2.Part__Feature.Edge15]
  Suppressed = false
  expr: .Offset2.Base.z = <<Revolute065>>.Offset2.Base.z
FEATURE [App::FeaturePython] Joint086  label="Fixed063"  # Assembly joint (typed FeaturePython)
  AngleMax = 0
  AngleMin = 0
  Detach1 = false
  Detach2 = false
  Distance = 0
  Distance2 = 0
  EnableAngleMax = false
  EnableAngleMin = false
  EnableLengthMax = false
  EnableLengthMin = false
  JointType = 0 (Fixed)
  LengthMax = 0
  LengthMin = 0
  Offset2 = pos=(0,0,1.5) rot=(0,0,1;3.14159rad)
  Placement1 = pos=(-8.46528,0.75,17) rot=(0,0.707107,0.707107;3.14159rad)
  Placement2 = pos=(8.44212,0.75,17) rot=(-1,0,0;1.5708rad)
  Reference1 = -> Assembly [Link021.Edge30,Link021.Edge30]
  Reference2 = -> Assembly [Link022.Edge36,Link022.Edge36]
  Suppressed = false
  expr: .Offset2.Base.z = Variables#Spreadsheet.WheelClampToShaftDist
FEATURE [Part::FeaturePython] Screw010  label="M4x30-Screw"  # WARN: FeaturePython — macro-defined, semantics opaque (R4)
  Diameter = 5
  Invert = false
  LeftHanded = false
  Length = 8
  LengthCustom = 30
  MatchOuter = false
  OffsetAngle = 0
  Placement = pos=(20.4333,47.758,-28.9634) rot=(0.404062,-0.001184,0.914731;3.13623rad)
  Thread = false
  Type = 74
FEATURE [App::FeaturePython] Joint087  label="Fixed064"  # Assembly joint (typed FeaturePython)
  AngleMax = 0
  AngleMin = 0
  Detach1 = false
  Detach2 = false
  Distance = 0
  Distance2 = 0
  EnableAngleMax = false
  EnableAngleMin = false
  EnableLengthMax = false
  EnableLengthMin = false
  JointType = 0 (Fixed)
  LengthMax = 0
  LengthMin = 0
  Placement2 = pos=(-8.46528,-13.75,17) rot=(0,0.707107,0.707107;3.14159rad)
  Reference1 = -> Assembly [Screw010.Edge26,Screw010.Edge26]
  Reference2 = -> Assembly [Wheel.Edge43,Wheel.Edge43]
  Suppressed = false
FEATURE [App::Link] Link027  label="M4x30-Screw001"
  LinkPlacement = pos=(9.04696,47.8247,-16.4652) rot=(0.404062,-0.001184,0.914731;3.13623rad)
  LinkedObject = -> Screw010
  Placement = pos=(9.04696,47.8247,-16.4652) rot=(0.404062,-0.001184,0.914731;3.13623rad)
FEATURE [App::FeaturePython] Joint088  label="Fixed065"  # Assembly joint (typed FeaturePython)
  AngleMax = 0
  AngleMin = 0
  Detach1 = false
  Detach2 = false
  Distance = 0
  Distance2 = 0
  EnableAngleMax = false
  EnableAngleMin = false
  EnableLengthMax = false
  EnableLengthMin = false
  JointType = 0 (Fixed)
  LengthMax = 0
  LengthMin = 0
  Placement2 = pos=(8.44212,-13.75,17) rot=(0,0.707107,0.707107;3.14159rad)
  Reference1 = -> Assembly [Link027.Edge26,Link027.Edge26]
  Reference2 = -> Assembly [Wheel.Edge46,Wheel.Edge46]
  Suppressed = false
FEATURE [App::FeaturePython] Joint004  label="Fixed002"  # Assembly joint (typed FeaturePython)
  AngleMax = 0
  AngleMin = 0
  Detach1 = false
  Detach2 = false
  Distance = 0
  Distance2 = 0
  EnableAngleMax = false
  EnableAngleMin = false
  EnableLengthMax = false
  EnableLengthMin = false
  JointType = 0 (Fixed)
  LengthMax = 0
  LengthMin = 0
  Placement1 = pos=(0,0,32.1564) rot=(0,0,1;0rad)
  Placement2 = pos=(-28,-50,-29) rot=(1,0,0;1.5708rad)
  Reference1 = -> Assembly [am_3637_NeveRest_Orbital_20_Gearmotor_REV2.Part__Feature.Edge163,am_3637_NeveRest_Orbital_20_Gearmotor_REV2.Part__Feature.Edge163]
  Reference2 = -> Assembly [Motor_Mount_Right.Edge28,Motor_Mount_Right.Edge28]
  Suppressed = false
FEATURE [App::FeaturePython] Joint089  label="Fixed"  # Assembly joint (typed FeaturePython)
  AngleMax = 0
  AngleMin = 0
  Detach1 = false
  Detach2 = false
  Distance = 0
  Distance2 = 0
  EnableAngleMax = false
  EnableAngleMin = false
  EnableLengthMax = false
  EnableLengthMin = false
  JointType = 0 (Fixed)
  LengthMax = 0
  LengthMin = 0
  Placement1 = pos=(3.6e-15,-50,13.75) rot=(1,0,0;1.5708rad)
  Placement2 = pos=(3.6e-15,-50,13.75) rot=(1,0,0;1.5708rad)
  Reference1 = -> Assembly [Body.Edge30,Body.Edge30]
  Reference2 = -> Assembly [Motor_Mount_Right.Edge36,Motor_Mount_Right.Edge36]
  Suppressed = false
FEATURE [App::FeaturePython] Joint090  label="Fixed066"  # Assembly joint (typed FeaturePython)
  AngleMax = 0
  AngleMin = 0
  Detach1 = false
  Detach2 = false
  Distance = 0
  Distance2 = 0
  EnableAngleMax = false
  EnableAngleMin = false
  EnableLengthMax = false
  EnableLengthMin = false
  JointType = 0 (Fixed)
  LengthMax = 0
  LengthMin = 0
  Placement1 = pos=(0,-50,13.75) rot=(1,0,0;1.5708rad)
  Placement2 = pos=(0,50,13.75) rot=(1,0,0;1.5708rad)
  Reference1 = -> Assembly [Link020.Edge36,Link020.Edge36]
  Reference2 = -> Assembly [Body.Edge59,Body.Edge59]
  Suppressed = false
FEATURE [App::Point] Origin005
  Role = Origin
FEATURE [Assembly::JointGroup] Joints002
FEATURE [Assembly::AssemblyObject] Assembly002
  Group = -> [Joints002]
  Origin = -> Origin004
  Type = Assembly
FEATURE [App::FeaturePython] Joint  label="Fixed067"  # Assembly joint (typed FeaturePython)
  AngleMax = 0
  AngleMin = 0
  Detach1 = false
  Detach2 = false
  Distance = 0
  Distance2 = 0
  EnableAngleMax = false
  EnableAngleMin = false
  EnableLengthMax = false
  EnableLengthMin = false
  JointType = 0 (Fixed)
  LengthMax = 0
  LengthMin = 0
  Placement2 = pos=(-37.5,-55,23.75) rot=(1,0,0;1.5708rad)
  Reference1 = -> Assembly [Screw004.Edge26,Screw004.Edge26]
  Reference2 = -> Assembly [Motor_Mount_Right.Edge69,Motor_Mount_Right.Edge69]
  Suppressed = false
FEATURE [App::FeaturePython] Joint091  label="Fixed068"  # Assembly joint (typed FeaturePython)
  AngleMax = 0
  AngleMin = 0
  Detach1 = false
  Detach2 = false
  Distance = 0
  Distance2 = 0
  EnableAngleMax = false
  EnableAngleMin = false
  EnableLengthMax = false
  EnableLengthMin = false
  JointType = 0 (Fixed)
  LengthMax = 0
  LengthMin = 0
  Placement1 = pos=(0,-55,13.75) rot=(1,0,0;1.5708rad)
  Reference1 = -> Assembly [Motor_Mount_Right.Edge72,Motor_Mount_Right.Edge72]
  Reference2 = -> Assembly [Screw006.Edge26,Screw006.Edge26]
  Suppressed = false
FEATURE [App::FeaturePython] Joint092  label="Fixed069"  # Assembly joint (typed FeaturePython)
  AngleMax = 0
  AngleMin = 0
  Detach1 = false
  Detach2 = false
  Distance = 0
  Distance2 = 0
  EnableAngleMax = false
  EnableAngleMin = false
  EnableLengthMax = false
  EnableLengthMin = false
  JointType = 0 (Fixed)
  LengthMax = 0
  LengthMin = 0
  Placement2 = pos=(-37.5,-55,3.75) rot=(1,0,0;1.5708rad)
  Reference1 = -> Assembly [Screw005.Edge26,Screw005.Edge26]
  Reference2 = -> Assembly [Motor_Mount_Right.Edge68,Motor_Mount_Right.Edge68]
  Suppressed = false
FEATURE [App::FeaturePython] Joint093  label="Fixed070"  # Assembly joint (typed FeaturePython)
  AngleMax = 0
  AngleMin = 0
  Detach1 = false
  Detach2 = false
  Distance = 0
  Distance2 = 0
  EnableAngleMax = false
  EnableAngleMin = false
  EnableLengthMax = false
  EnableLengthMin = false
  JointType = 0 (Fixed)
  LengthMax = 0
  LengthMin = 0
  Placement2 = pos=(37.5,-55,23.75) rot=(1,0,0;1.5708rad)
  Reference1 = -> Assembly [Link001.Edge26,Link001.Edge26]
  Reference2 = -> Assembly [Motor_Mount_Right.Edge75,Motor_Mount_Right.Edge75]
  Suppressed = false
FEATURE [App::FeaturePython] Joint094  label="Fixed071"  # Assembly joint (typed FeaturePython)
  AngleMax = 0
  AngleMin = 0
  Detach1 = false
  Detach2 = false
  Distance = 0
  Distance2 = 0
  EnableAngleMax = false
  EnableAngleMin = false
  EnableLengthMax = false
  EnableLengthMin = false
  JointType = 0 (Fixed)
  LengthMax = 0
  LengthMin = 0
  Placement2 = pos=(37.5,-55,3.75) rot=(1,0,0;1.5708rad)
  Reference1 = -> Assembly [Screw007.Edge26,Screw007.Edge26]
  Reference2 = -> Assembly [Motor_Mount_Right.Edge74,Motor_Mount_Right.Edge74]
  Suppressed = false
FEATURE [App::FeaturePython] Joint095  label="Fixed072"  # Assembly joint (typed FeaturePython)
  AngleMax = 0
  AngleMin = 0
  Detach1 = false
  Detach2 = false
  Distance = 0
  Distance2 = 0
  EnableAngleMax = false
  EnableAngleMin = false
  EnableLengthMax = false
  EnableLengthMin = false
  JointType = 0 (Fixed)
  LengthMax = 0
  LengthMin = 0
  Placement2 = pos=(37.5,-55,23.75) rot=(1,0,0;1.5708rad)
  Reference1 = -> Assembly [Link015.Edge26,Link015.Edge26]
  Reference2 = -> Assembly [Link020.Edge75,Link020.Edge75]
  Suppressed = false
FEATURE [App::FeaturePython] Joint096  label="Fixed073"  # Assembly joint (typed FeaturePython)
  AngleMax = 0
  AngleMin = 0
  Detach1 = false
  Detach2 = false
  Distance = 0
  Distance2 = 0
  EnableAngleMax = false
  EnableAngleMin = false
  EnableLengthMax = false
  EnableLengthMin = false
  JointType = 0 (Fixed)
  LengthMax = 0
  LengthMin = 0
  Placement2 = pos=(37.5,-55,3.75) rot=(1,0,0;1.5708rad)
  Reference1 = -> Assembly [Link017.Edge26,Link017.Edge26]
  Reference2 = -> Assembly [Link020.Edge74,Link020.Edge74]
  Suppressed = false
FEATURE [App::FeaturePython] Joint097  label="Fixed074"  # Assembly joint (typed FeaturePython)
  AngleMax = 0
  AngleMin = 0
  Detach1 = false
  Detach2 = false
  Distance = 0
  Distance2 = 0
  EnableAngleMax = false
  EnableAngleMin = false
  EnableLengthMax = false
  EnableLengthMin = false
  JointType = 0 (Fixed)
  LengthMax = 0
  LengthMin = 0
  Placement2 = pos=(3.6e-15,-55,13.75) rot=(1,0,0;1.5708rad)
  Reference1 = -> Assembly [Link014.Edge26,Link014.Edge26]
  Reference2 = -> Assembly [Link020.Edge72,Link020.Edge72]
  Suppressed = false
FEATURE [App::FeaturePython] Joint098  label="Fixed075"  # Assembly joint (typed FeaturePython)
  AngleMax = 0
  AngleMin = 0
  Detach1 = false
  Detach2 = false
  Distance = 0
  Distance2 = 0
  EnableAngleMax = false
  EnableAngleMin = false
  EnableLengthMax = false
  EnableLengthMin = false
  JointType = 0 (Fixed)
  LengthMax = 0
  LengthMin = 0
  Placement2 = pos=(-37.5,-55,23.75) rot=(1,0,0;1.5708rad)
  Reference1 = -> Assembly [Link018.Edge26,Link018.Edge26]
  Reference2 = -> Assembly [Link020.Edge69,Link020.Edge69]
  Suppressed = false
FEATURE [App::FeaturePython] Joint099  label="Fixed076"  # Assembly joint (typed FeaturePython)
  AngleMax = 0
  AngleMin = 0
  Detach1 = false
  Detach2 = false
  Distance = 0
  Distance2 = 0
  EnableAngleMax = false
  EnableAngleMin = false
  EnableLengthMax = false
  EnableLengthMin = false
  JointType = 0 (Fixed)
  LengthMax = 0
  LengthMin = 0
  Placement2 = pos=(-37.5,-55,3.75) rot=(1,0,0;1.5708rad)
  Reference1 = -> Assembly [Link016.Edge26,Link016.Edge26]
  Reference2 = -> Assembly [Link020.Edge68,Link020.Edge68]
  Suppressed = false
FEATURE [App::Link] Bearing_Wheel_Mount  label="Bearing Wheel Mount"
  LinkPlacement = pos=(-23.8603,-24.6888,-3.00006) rot=(0,0,-1;0.005858rad)
  LinkedObject = -> <external Body/Body.FCStd>#Body004
  Placement = pos=(-23.8603,-24.6888,-3.00006) rot=(0,0,-1;0.005858rad)
FEATURE [App::FeaturePython] Joint100  label="Fixed077"  # Assembly joint (typed FeaturePython)
  AngleMax = 0
  AngleMin = 0
  Detach1 = false
  Detach2 = false
  Distance = 0
  Distance2 = 0
  EnableAngleMax = false
  EnableAngleMin = false
  EnableLengthMax = false
  EnableLengthMin = false
  JointType = 0 (Fixed)
  LengthMax = 0
  LengthMin = 0
  Offset2 = pos=(0,0,0) rot=(0,0,1;3.14159rad)
  Placement1 = pos=(3.77684,-45,-21.9121) rot=(0,0.707107,0.707107;3.14159rad)
  Placement2 = pos=(3.77684,-55,-21.9121) rot=(0,-0.707107,0.707107;3.14159rad)
  Reference1 = -> Assembly [Bearing_Wheel_Mount.Edge47,Bearing_Wheel_Mount.Edge47]
  Reference2 = -> Assembly [Motor_Mount_Right.Edge70,Motor_Mount_Right.Edge70]
  Suppressed = false
FEATURE [App::Link] Link028  label="Bearing Wheel Mount001"
  LinkPlacement = pos=(-23.7431,-4.68909,-3.00006) rot=(0,0,1;3.13573rad)
  LinkedObject = -> Bearing_Wheel_Mount
  Placement = pos=(-23.7431,-4.68909,-3.00006) rot=(0,0,1;3.13573rad)
FEATURE [App::FeaturePython] Joint101  label="Fixed078"  # Assembly joint (typed FeaturePython)
  AngleMax = 0
  AngleMin = 0
  Detach1 = false
  Detach2 = false
  Distance = 0
  Distance2 = 0
  EnableAngleMax = false
  EnableAngleMin = false
  EnableLengthMax = false
  EnableLengthMin = false
  JointType = 0 (Fixed)
  LengthMax = 0
  LengthMin = 0
  Offset2 = pos=(0,0,0) rot=(0,0,1;3.14159rad)
  Placement1 = pos=(3.77684,-45,-21.9121) rot=(0,-0.707107,-0.707107;3.14159rad)
  Placement2 = pos=(3.77684,-55,-21.9121) rot=(0,-0.707107,0.707107;3.14159rad)
  Reference1 = -> Assembly [Link028.Edge47,Link028.Edge47]
  Reference2 = -> Assembly [Link020.Edge70,Link020.Edge70]
  Suppressed = false
FEATURE [Part::FeaturePython] Screw011  label="M4x25-Screw"  # WARN: FeaturePython — macro-defined, semantics opaque (R4)
  Diameter = 5
  Invert = false
  LeftHanded = false
  Length = 7
  LengthCustom = 25
  MatchOuter = false
  OffsetAngle = 0
  Placement = pos=(-22.4694,-68.1976,-0.592235) rot=(0.999991,-0.002929,0.002929;4.71238rad)
  Thread = false
  Type = 74
FEATURE [App::Link] Link029  label="M4x16-Screw119"
  LinkPlacement = pos=(-48.7139,38.9579,-6.9141) rot=(0.002071,0.707105,-0.707105;3.14574rad)
  LinkedObject = -> Screw011
  Placement = pos=(-48.7139,38.9579,-6.9141) rot=(0.002071,0.707105,-0.707105;3.14574rad)
FEATURE [App::Link] Link030  label="M4x16-Screw120"
  LinkPlacement = pos=(-25.1339,38.8198,-0.592235) rot=(0.002071,0.707105,-0.707105;3.14574rad)
  LinkedObject = -> Link029
  Placement = pos=(-25.1339,38.8198,-0.592235) rot=(0.002071,0.707105,-0.707105;3.14574rad)
FEATURE [App::Link] Link031  label="M4x16-Screw121"
  LinkPlacement = pos=(1.11053,-68.3358,-6.9141) rot=(0.999991,-0.002929,0.002929;4.71238rad)
  LinkedObject = -> Link030
  Placement = pos=(1.11053,-68.3358,-6.9141) rot=(0.999991,-0.002929,0.002929;4.71238rad)
FEATURE [Part::FeaturePython] Screw012  label="M4x25-Screw002"  # WARN: FeaturePython — macro-defined, semantics opaque (R4)
  Diameter = 5
  Invert = false
  LeftHanded = false
  Length = 7
  LengthCustom = 25
  MatchOuter = false
  OffsetAngle = 0
  Placement = pos=(-27.2855,35.3323,-24.9122) rot=(-0.002071,-0.707105,0.707105;3.13745rad)
  Thread = false
  Type = 74
FEATURE [App::Link] Link032  label="M4x16-Screw123"
  LinkPlacement = pos=(-20.3178,-64.7102,-24.9122) rot=(-0.999991,0.002929,-0.002929;1.57081rad)
  LinkedObject = -> Screw012
  Placement = pos=(-20.3178,-64.7102,-24.9122) rot=(-0.999991,0.002929,-0.002929;1.57081rad)
FEATURE [App::FeaturePython] Joint102  label="Fixed079"  # Assembly joint (typed FeaturePython)
  AngleMax = 0
  AngleMin = 0
  Detach1 = false
  Detach2 = false
  Distance = 0
  Distance2 = 0
  EnableAngleMax = false
  EnableAngleMin = false
  EnableLengthMax = false
  EnableLengthMin = false
  JointType = 0 (Fixed)
  LengthMax = 0
  LengthMin = 0
  Placement2 = pos=(1.64571,-53.5,2.40782) rot=(-1,0,0;1.5708rad)
  Reference1 = -> Assembly [Screw011.Edge26,Screw011.Edge26]
  Reference2 = -> Assembly [Motor_Mount_Right.Edge137,Motor_Mount_Right.Edge137]
  Suppressed = false
FEATURE [App::FeaturePython] Joint105  label="Fixed082"  # Assembly joint (typed FeaturePython)
  AngleMax = 0
  AngleMin = 0
  Detach1 = false
  Detach2 = false
  Distance = 0
  Distance2 = 0
  EnableAngleMax = false
  EnableAngleMin = false
  EnableLengthMax = false
  EnableLengthMin = false
  JointType = 0 (Fixed)
  LengthMax = 0
  LengthMin = 0
  Placement2 = pos=(1.64571,-53.5,2.40782) rot=(1,0,0;4.71239rad)
  Reference1 = -> Assembly [Link030.Edge26,Link030.Edge26]
  Reference2 = -> Assembly [Link020.Edge137,Link020.Edge137]
  Suppressed = false
FEATURE [App::FeaturePython] Joint106  label="Fixed083"  # Assembly joint (typed FeaturePython)
  AngleMax = 0
  AngleMin = 0
  Detach1 = false
  Detach2 = false
  Distance = 0
  Distance2 = 0
  EnableAngleMax = false
  EnableAngleMin = false
  EnableLengthMax = false
  EnableLengthMin = false
  JointType = 0 (Fixed)
  LengthMax = 0
  LengthMin = 0
  Placement2 = pos=(3.77684,-50,-21.9121) rot=(1,0,0;1.5708rad)
  Reference1 = -> Assembly [Screw012.Edge26,Screw012.Edge26]
  Reference2 = -> Assembly [Link020.Edge34,Link020.Edge34]
  Suppressed = false
FEATURE [App::FeaturePython] Joint107  label="Fixed084"  # Assembly joint (typed FeaturePython)
  AngleMax = 0
  AngleMin = 0
  Detach1 = false
  Detach2 = false
  Distance = 0
  Distance2 = 0
  EnableAngleMax = false
  EnableAngleMin = false
  EnableLengthMax = false
  EnableLengthMin = false
  JointType = 0 (Fixed)
  LengthMax = 0
  LengthMin = 0
  Placement2 = pos=(3.77684,-50,-21.9121) rot=(1,0,0;1.5708rad)
  Reference1 = -> Assembly [Link032.Edge26,Link032.Edge26]
  Reference2 = -> Assembly [Motor_Mount_Right.Edge34,Motor_Mount_Right.Edge34]
  Suppressed = false
FEATURE [App::FeaturePython] Joint108  label="Fixed085"  # Assembly joint (typed FeaturePython)
  AngleMax = 0
  AngleMin = 0
  Detach1 = false
  Detach2 = false
  Distance = 0
  Distance2 = 0
  EnableAngleMax = false
  EnableAngleMin = false
  EnableLengthMax = false
  EnableLengthMin = false
  JointType = 0 (Fixed)
  LengthMax = 0
  LengthMin = 0
  Placement2 = pos=(25.2261,-53.5,-3.91404) rot=(-1,0,0;1.5708rad)
  Reference1 = -> Assembly [Link031.Edge26,Link031.Edge26]
  Reference2 = -> Assembly [Motor_Mount_Right.Edge11,Motor_Mount_Right.Edge11]
  Suppressed = false
FEATURE [App::FeaturePython] Joint109  label="Fixed086"  # Assembly joint (typed FeaturePython)
  AngleMax = 0
  AngleMin = 0
  Detach1 = false
  Detach2 = false
  Distance = 0
  Distance2 = 0
  EnableAngleMax = false
  EnableAngleMin = false
  EnableLengthMax = false
  EnableLengthMin = false
  JointType = 0 (Fixed)
  LengthMax = 0
  LengthMin = 0
  Placement2 = pos=(25.2261,-53.5,-3.91404) rot=(1,0,0;4.71239rad)
  Reference1 = -> Assembly [Link029.Edge30,Link029.Edge30]
  Reference2 = -> Assembly [Link020.Edge11,Link020.Edge11]
  Suppressed = false
FEATURE [App::FeaturePython] Joint110  label="Fixed087"  # Assembly joint (typed FeaturePython)
  AngleMax = 0
  AngleMin = 0
  Detach1 = false
  Detach2 = false
  Distance = 0
  Distance2 = 0
  EnableAngleMax = false
  EnableAngleMin = false
  EnableLengthMax = false
  EnableLengthMin = false
  JointType = 0 (Fixed)
  LengthMax = 0
  LengthMin = 0
  Placement2 = pos=(37.5,45,3.75) rot=(0,-0.707107,0.707107;3.14159rad)
  Reference1 = -> Assembly [Link008.Edge27,Link008.Edge27]
  Reference2 = -> Assembly [Body.Face19,Body.Edge16]
  Suppressed = false
FEATURE [App::FeaturePython] Joint111  label="Fixed088"  # Assembly joint (typed FeaturePython)
  AngleMax = 0
  AngleMin = 0
  Detach1 = false
  Detach2 = false
  Distance = 0
  Distance2 = 0
  EnableAngleMax = false
  EnableAngleMin = false
  EnableLengthMax = false
  EnableLengthMin = false
  JointType = 0 (Fixed)
  LengthMax = 0
  LengthMin = 0
  Placement1 = pos=(-3.6e-15,1.8e-15,3.2) rot=(0,0,1;0rad)
  Placement2 = pos=(3.6e-15,45,13.75) rot=(1,0,0;1.5708rad)
  Reference1 = -> Assembly [Link004.Edge2,Link004.Edge2]
  Reference2 = -> Assembly [Body.Edge131,Body.Edge131]
  Suppressed = false
FEATURE [App::FeaturePython] Joint112  label="Fixed089"  # Assembly joint (typed FeaturePython)
  AngleMax = 0
  AngleMin = 0
  Detach1 = false
  Detach2 = false
  Distance = 0
  Distance2 = 0
  EnableAngleMax = false
  EnableAngleMin = false
  EnableLengthMax = false
  EnableLengthMin = false
  JointType = 0 (Fixed)
  LengthMax = 0
  LengthMin = 0
  Placement1 = pos=(7.1e-15,-2e-16,3.2) rot=(0,0,1;0rad)
  Placement2 = pos=(-37.5,45,3.75) rot=(1,0,0;1.5708rad)
  Reference1 = -> Assembly [Link005.Edge2,Link005.Edge2]
  Reference2 = -> Assembly [Body.Edge133,Body.Edge133]
  Suppressed = false
FEATURE [App::FeaturePython] Joint113  label="Fixed090"  # Assembly joint (typed FeaturePython)
  AngleMax = 0
  AngleMin = 0
  Detach1 = false
  Detach2 = false
  Distance = 0
  Distance2 = 0
  EnableAngleMax = false
  EnableAngleMin = false
  EnableLengthMax = false
  EnableLengthMin = false
  JointType = 0 (Fixed)
  LengthMax = 0
  LengthMin = 0
  Placement1 = pos=(1.8e-15,0,3.2) rot=(0,0,1;0rad)
  Placement2 = pos=(70,25,5) rot=(0.57735,0.57735,0.57735;2.0944rad)
  Reference1 = -> Assembly [Link012.Edge2,Link012.Edge2]
  Reference2 = -> Assembly [Body.Edge112,Body.Edge112]
  Suppressed = false
FEATURE [App::FeaturePython] Joint114  label="Fixed091"  # Assembly joint (typed FeaturePython)
  AngleMax = 0
  AngleMin = 0
  Detach1 = false
  Detach2 = false
  Distance = 0
  Distance2 = 0
  EnableAngleMax = false
  EnableAngleMin = false
  EnableLengthMax = false
  EnableLengthMin = false
  JointType = 0 (Fixed)
  LengthMax = 0
  LengthMin = 0
  Placement1 = pos=(1.8e-15,0,3.2) rot=(0,0,1;0rad)
  Placement2 = pos=(70,25,30) rot=(0.57735,0.57735,0.57735;2.0944rad)
  Reference1 = -> Assembly [Link013.Edge2,Link013.Edge2]
  Reference2 = -> Assembly [Body.Edge110,Body.Edge110]
  Suppressed = false
FEATURE [App::FeaturePython] Joint115  label="Fixed092"  # Assembly joint (typed FeaturePython)
  AngleMax = 0
  AngleMin = 0
  Detach1 = false
  Detach2 = false
  Distance = 0
  Distance2 = 0
  EnableAngleMax = false
  EnableAngleMin = false
  EnableLengthMax = false
  EnableLengthMin = false
  JointType = 0 (Fixed)
  LengthMax = 0
  LengthMin = 0
  Placement1 = pos=(7.1e-15,0,3.2) rot=(0,0,1;0rad)
  Placement2 = pos=(70,-25,30) rot=(0.57735,0.57735,0.57735;2.0944rad)
  Reference1 = -> Assembly [Link010.Edge2,Link010.Edge2]
  Reference2 = -> Assembly [Body.Edge109,Body.Edge109]
  Suppressed = false
FEATURE [App::Link] Link033  label="1609-0613-0008"
  LinkPlacement = pos=(41.3026,2.92997,49.9999) rot=(0.002929,0.999991,0.002929;4.71238rad)
  LinkedObject = -> _609_0613_0007
  Placement = pos=(41.3026,2.92997,49.9999) rot=(0.002929,0.999991,0.002929;4.71238rad)
FEATURE [App::Link] Link034  label="StringGuard001"
  LinkPlacement = pos=(41.3041,3.17997,49.9999) rot=(0.002929,0.999996,0;3.14159rad)
  LinkedObject = -> StringGuard
  Placement = pos=(41.3041,3.17997,49.9999) rot=(0.002929,0.999996,0;3.14159rad)
FEATURE [App::FeaturePython] Joint116  label="Fixed093"  # Assembly joint (typed FeaturePython)
  AngleMax = 0
  AngleMin = 0
  Detach1 = false
  Detach2 = false
  Distance = 0
  Distance2 = 0
  EnableAngleMax = false
  EnableAngleMin = false
  EnableLengthMax = false
  EnableLengthMin = false
  JointType = 0 (Fixed)
  LengthMax = 0
  LengthMin = 0
  Placement1 = pos=(7.1e-15,-3.25,0) rot=(1,0,0;1.5708rad)
  Placement2 = pos=(65,15,53) rot=(0,0.707107,0.707107;3.14159rad)
  Reference1 = -> Assembly [Link034.Edge9,Link034.Edge9]
  Reference2 = -> Assembly [Slides_Mount.Edge100,Slides_Mount.Edge100]
  Suppressed = false
FEATURE [App::FeaturePython] Joint117  label="Fixed094"  # Assembly joint (typed FeaturePython)
  AngleMax = 0
  AngleMin = 0
  Detach1 = false
  Detach2 = false
  Distance = 0
  Distance2 = 0
  EnableAngleMax = false
  EnableAngleMin = false
  EnableLengthMax = false
  EnableLengthMin = false
  JointType = 0 (Fixed)
  LengthMax = 0
  LengthMin = 0
  Placement1 = pos=(0,0,0) rot=(0.57735,-0.57735,0.57735;2.0944rad)
  Placement2 = pos=(7.1e-15,-0.25,0) rot=(1,0,0;1.5708rad)
  Reference1 = -> Assembly [Link033.Part__Feature002.Edge103,Link033.Part__Feature002.Edge103]
  Reference2 = -> Assembly [Link034.Edge4,Link034.Edge4]
  Suppressed = false
FEATURE [App::Link] Battery_Mount  label="Battery Mount"
  LinkPlacement = pos=(-153.799,-13.9273,-3.00006) rot=(0,0,1;3.13573rad)
  LinkedObject = -> <external Body/Body.FCStd>#Body007
  Placement = pos=(-153.799,-13.9273,-3.00006) rot=(0,0,1;3.13573rad)
FEATURE [App::FeaturePython] Joint118  label="Fixed095"  # Assembly joint (typed FeaturePython)
  AngleMax = 0
  AngleMin = 0
  Detach1 = false
  Detach2 = false
  Distance = 0
  Distance2 = 0
  EnableAngleMax = false
  EnableAngleMin = false
  EnableLengthMax = false
  EnableLengthMin = false
  JointType = 0 (Fixed)
  LengthMax = 0
  LengthMin = 0
  Offset2 = pos=(0,0,0) rot=(0,0,-1;1.5708rad)
  Placement1 = pos=(-65,12.5,40) rot=(0,0,-1;4.71239rad)
  Placement2 = pos=(-65,-12.5,40) rot=(0,0,-1;1.5708rad)
  Reference1 = -> Assembly [Battery_Mount.Edge17,Battery_Mount.Edge17]
  Reference2 = -> Assembly [Body_Top.Edge32,Body_Top.Edge32]
  Suppressed = false
FEATURE [App::Link] GUNCAIZHU_Ventilator_30x30x7_5_5V014  label="GUNCAIZHU_Ventilator_30x30x7,5_5V014"
  LinkPlacement = pos=(30.3771,-27.0065,34.7999) rot=(0.002929,0.999991,-0.002929;1.57081rad)
  LinkedObject = -> <external Imports/Fan.FCStd>#GUNCAIZHU_Ventilator_30x30x7_5_5V
  Placement = pos=(30.3771,-27.0065,34.7999) rot=(0.002929,0.999991,-0.002929;1.57081rad)
FEATURE [App::FeaturePython] Joint119  label="Fixed096"  # Assembly joint (typed FeaturePython)
  AngleMax = 0
  AngleMin = 0
  Detach1 = false
  Detach2 = false
  Distance = 0
  Distance2 = 0
  EnableAngleMax = false
  EnableAngleMin = false
  EnableLengthMax = false
  EnableLengthMin = false
  JointType = 0 (Fixed)
  LengthMax = 0
  LengthMin = 0
  Placement1 = pos=(1.8,-11.9,11.9) rot=(0.707107,0,0.707107;3.14159rad)
  Placement2 = pos=(66.15,-23.9,36) rot=(1,0,0;3.14159rad)
  Reference1 = -> Assembly [GUNCAIZHU_Ventilator_30x30x7_5_5V014.Part__Feature.Edge4,GUNCAIZHU_Ventilator_30x30x7_5_5V014.Part__Feature.Edge4]
  Reference2 = -> Assembly [Body_Top.Edge125,Body_Top.Edge125]
  Suppressed = false
FEATURE [App::Link] Slides_Motor_Mount  label="Slides Motor Mount"
  LinkPlacement = pos=(-18.8604,-24.718,71.9999) rot=(0,0,1;4.70653rad)
  LinkedObject = -> <external Slides Motor Mount/SlidesMotorMount.FCStd>#Body
  Placement = pos=(-18.8604,-24.718,71.9999) rot=(0,0,1;4.70653rad)
FEATURE [App::FeaturePython] Joint122  label="Fixed099"  # Assembly joint (typed FeaturePython)
  AngleMax = 0
  AngleMin = 0
  Detach1 = false
  Detach2 = false
  Distance = 0
  Distance2 = 0
  EnableAngleMax = false
  EnableAngleMin = false
  EnableLengthMax = false
  EnableLengthMin = false
  JointType = 0 (Fixed)
  LengthMax = 0
  LengthMin = 0
  Placement1 = pos=(30,-22.5,-35) rot=(-0.707107,-0.707107,0;3.14159rad)
  Placement2 = pos=(-17.5,-40,40) rot=(0,0,1;0rad)
  Reference1 = -> Assembly [Slides_Motor_Mount.Edge57,Slides_Motor_Mount.Edge57]
  Reference2 = -> Assembly [Body_Top.Edge35,Body_Top.Edge35]
  Suppressed = false
FEATURE [App::Link] Link035  label="am-3637 NeveRest Orbital 20 Gearmotor REV004"
  LinkPlacement = pos=(9.7793,-59.7045,59.5579) rot=(0.999991,-0.002929,0.002929;4.71238rad)
  LinkedObject = -> am_3637_NeveRest_Orbital_20_Gearmotor_REV2
  Placement = pos=(9.7793,-59.7045,59.5579) rot=(0.999991,-0.002929,0.002929;4.71238rad)
FEATURE [App::FeaturePython] Joint123  label="Fixed100"  # Assembly joint (typed FeaturePython)
  AngleMax = 0
  AngleMin = 0
  Detach1 = false
  Detach2 = false
  Distance = 0
  Distance2 = 0
  EnableAngleMax = false
  EnableAngleMin = false
  EnableLengthMax = false
  EnableLengthMin = false
  JointType = 0 (Fixed)
  LengthMax = 0
  LengthMin = 0
  Placement1 = pos=(0,0,32.1564) rot=(0,0,1;0rad)
  Placement2 = pos=(5,3.6e-15,-2.84e-14) rot=(-0.57735,-0.57735,-0.57735;4.18879rad)
  Reference1 = -> Assembly [Link035.Part__Feature.Edge165,Link035.Part__Feature.Edge165]
  Reference2 = -> Assembly [Slides_Motor_Mount.Edge61,Slides_Motor_Mount.Edge61]
  Suppressed = false
FEATURE [App::Link] Spool
  LinkPlacement = pos=(-18.7889,-12.5133,71.9999) rot=(-0.999983,0.005858,0;1.5708rad)
  LinkedObject = -> <external Spool/Spool.FCStd>#Body
  Placement = pos=(-18.7889,-12.5133,71.9999) rot=(-0.999983,0.005858,0;1.5708rad)
FEATURE [App::Link] Spool_CHub  label="Spool CHub"
  LinkPlacement = pos=(-18.7889,-12.5133,71.9999) rot=(-0.999983,0.005858,0;1.5708rad)
  LinkedObject = -> <external Spool/Spool.FCStd>#Body001
  Placement = pos=(-18.7889,-12.5133,71.9999) rot=(-0.999983,0.005858,0;1.5708rad)
FEATURE [App::FeaturePython] Joint124  label="Fixed101"  # Assembly joint (typed FeaturePython)
  AngleMax = 0
  AngleMin = 0
  Detach1 = false
  Detach2 = false
  Distance = 0
  Distance2 = 0
  EnableAngleMax = false
  EnableAngleMin = false
  EnableLengthMax = false
  EnableLengthMin = false
  JointType = 0 (Fixed)
  LengthMax = 0
  LengthMin = 0
  Placement1 = pos=(9,5,0) rot=(0,0,1;0rad)
  Placement2 = pos=(9,5,0) rot=(1,0,0;3.14159rad)
  Reference1 = -> Assembly [Spool.Edge45,Spool.Edge45]
  Reference2 = -> Assembly [Spool_CHub.Edge22,Spool_CHub.Edge22]
  Suppressed = false
FEATURE [App::FeaturePython] Joint125  label="Revolute102"  # Assembly joint (typed FeaturePython)
  AngleMax = 0
  AngleMin = 0
  Detach1 = false
  Detach2 = false
  Distance = 0
  Distance2 = 0
  EnableAngleMax = false
  EnableAngleMin = false
  EnableLengthMax = false
  EnableLengthMin = false
  JointType = 1 (Revolute)
  LengthMax = 0
  LengthMin = 0
  Offset2 = pos=(0,0,5) rot=(0,0,1;0rad)
  Placement1 = pos=(0,0,-9) rot=(1,0,0;3.14159rad)
  Placement2 = pos=(0,0,40.3614) rot=(0,0,1;0rad)
  Reference1 = -> Assembly [Spool_CHub.Edge33,Spool_CHub.Edge33]
  Reference2 = -> Assembly [Link035.Part__Feature.Edge218,Link035.Part__Feature.Edge218]
  Suppressed = false
FEATURE [App::Link] Passive_Claw_Left  label="Passive Claw Left"
  LinkPlacement = pos=(94.6084,-30.3829,-65.5001) rot=(0,0,1;4.70653rad)
  LinkedObject = -> <external Passive Claw/PassiveClaw.FCStd>#Part__Mirroring
  Placement = pos=(94.6084,-30.3829,-65.5001) rot=(0,0,1;4.70653rad)
FEATURE [App::Link] Passive_Claw_Right  label="Passive Claw Right"
  LinkPlacement = pos=(94.5498,-40.3827,-65.5001) rot=(0,0,1;4.70653rad)
  LinkedObject = -> <external Passive Claw/PassiveClaw.FCStd>#Body
  Placement = pos=(94.5498,-40.3827,-65.5001) rot=(0,0,1;4.70653rad)
FEATURE [App::FeaturePython] Joint126  label="Fixed102"  # Assembly joint (typed FeaturePython)
  AngleMax = 0
  AngleMin = 0
  Detach1 = false
  Detach2 = false
  Distance = 0
  Distance2 = 0
  EnableAngleMax = false
  EnableAngleMin = false
  EnableLengthMax = false
  EnableLengthMin = false
  JointType = 0 (Fixed)
  LengthMax = 0
  LengthMin = 0
  Placement1 = pos=(19,-8,0) rot=(0,0,1;0rad)
  Placement2 = pos=(-6,-25.5,17) rot=(1,0,0;1.5708rad)
  Reference1 = -> Assembly [Slides_Plate.Edge27,Slides_Plate.Edge27]
  Reference2 = -> Assembly [Passive_Claw_Right.Edge57,Passive_Claw_Right.Edge57]
  Suppressed = false
FEATURE [App::FeaturePython] Joint127  label="Fixed103"  # Assembly joint (typed FeaturePython)
  AngleMax = 0
  AngleMin = 0
  Detach1 = false
  Detach2 = false
  Distance = 0
  Distance2 = 0
  EnableAngleMax = false
  EnableAngleMin = false
  EnableLengthMax = false
  EnableLengthMin = false
  JointType = 0 (Fixed)
  LengthMax = 0
  LengthMin = 0
  Offset2 = pos=(0,0,0) rot=(0,0,1;3.14159rad)
  Placement1 = pos=(-31,-8,1.42e-14) rot=(0,0,1;0rad)
  Placement2 = pos=(-46,-25.5,17) rot=(-1,0,0;1.5708rad)
  Reference1 = -> Assembly [Slides_Plate.Edge30,Slides_Plate.Edge30]
  Reference2 = -> Assembly [Passive_Claw_Left.Edge58,Passive_Claw_Left.Edge58]
  Suppressed = false
FEATURE [App::Link] Cat_Toy_Mount  label="Cat Toy Mount"
  LinkPlacement = pos=(-23.8017,-14.6889,-3.00006) rot=(0,0,1;3.13573rad)
  LinkedObject = -> <external Body/Body.FCStd>#Body008
  Placement = pos=(-23.8017,-14.6889,-3.00006) rot=(0,0,1;3.13573rad)
FEATURE [App::FeaturePython] Joint128  label="Fixed104"  # Assembly joint (typed FeaturePython)
  AngleMax = 0
  AngleMin = 0
  Detach1 = false
  Detach2 = false
  Distance = 0
  Distance2 = 0
  EnableAngleMax = false
  EnableAngleMin = false
  EnableLengthMax = false
  EnableLengthMin = false
  JointType = 0 (Fixed)
  LengthMax = 0
  LengthMin = 0
  Offset2 = pos=(0,0,0) rot=(0,0,1;3.14159rad)
  Placement1 = pos=(-66,41,40) rot=(0,0,1;0rad)
  Placement2 = pos=(66,-41,40) rot=(0,0,1;3.14159rad)
  Reference1 = -> Assembly [Body_Top.Edge30,Body_Top.Edge30]
  Reference2 = -> Assembly [Cat_Toy_Mount.Edge123,Cat_Toy_Mount.Edge123]
  Suppressed = false
FEATURE [App::Link] Cat_Toy_Clamp  label="Cat Toy Clamp"
  LinkPlacement = pos=(-23.8017,-14.6889,-3.00006) rot=(0,0,1;3.13573rad)
  LinkedObject = -> <external Body/Body.FCStd>#Body009
  Placement = pos=(-23.8017,-14.6889,-3.00006) rot=(0,0,1;3.13573rad)
FEATURE [App::FeaturePython] Joint129  label="Slider001"  # Assembly joint (typed FeaturePython)
  AngleMax = 0
  AngleMin = 0
  Detach1 = false
  Detach2 = false
  Distance = 0
  Distance2 = 0
  EnableAngleMax = false
  EnableAngleMin = false
  EnableLengthMax = false
  EnableLengthMin = false
  JointType = 3 (Slider)
  LengthMax = 0
  LengthMin = 0
  Placement1 = pos=(95.75,-10.0999,28.2) rot=(0.57735,0.57735,0.57735;2.0944rad)
  Placement2 = pos=(93.75,-10.0999,28.2) rot=(0.57735,0.57735,0.57735;2.0944rad)
  Reference1 = -> Assembly [Cat_Toy_Clamp.Edge80,Cat_Toy_Clamp.Edge80]
  Reference2 = -> Assembly [Cat_Toy_Mount.Edge9,Cat_Toy_Mount.Edge9]
  Suppressed = false
FEATURE [App::FeaturePython] Joint130  label="Distance"  # Assembly joint (typed FeaturePython)
  AngleMax = 0
  AngleMin = 0
  Detach1 = false
  Detach2 = false
  Distance = 0
  Distance2 = 0
  EnableAngleMax = false
  EnableAngleMin = false
  EnableLengthMax = false
  EnableLengthMin = false
  JointType = 5 (Distance)
  LengthMax = 0
  LengthMin = 0
  Placement1 = pos=(109,1.8e-15,5) rot=(0.57735,0.57735,0.57735;2.0944rad)
  Placement2 = pos=(109,0,42.5) rot=(0.57735,0.57735,0.57735;2.0944rad)
  Reference1 = -> Assembly [Cat_Toy_Clamp.Face29,Cat_Toy_Clamp.Face29]
  Reference2 = -> Assembly [Cat_Toy_Mount.Face13,Cat_Toy_Mount.Face13]
  Suppressed = false
FEATURE [Assembly::JointGroup] Joints
  Group = -> [Joint004,Joint009,Joint012,Joint013,Joint014,Joint015,Joint023,Joint027,Joint028,Joint029,Joint031,Joint034,Joint037,GroundedJoint,Joint045,Joint046,Joint047,Joint053,Joint054,Joint055,Joint056,Joint081,Joint082,Joint083,Joint084,Joint085,Joint086,Joint087,Joint088,Joint089,Joint090,Joint,Joint091,Joint092,Joint093,Joint094,Joint095,Joint096,Joint097,Joint098,Joint099,Joint100,Joint101,Joint102,+24 more]
FEATURE [Assembly::AssemblyObject] Assembly  label="Robot Assembly"
  Group = -> [Joints,Body,am_3637_NeveRest_Orbital_20_Gearmotor_REV2,Motor_Mount_Right,Joint004,Link,Slides_Mount,Joint009,Screw,Joint012,Screw001,Screw002,Screw003,Joint013,Joint014,Joint015,Screw004,Screw005,Screw006,Screw007,Link001,Ras_Pi_3B_179,Link002,Screw008,Nut,Joint023,Joint027,Body_Top,Joint028,Nut001,Joint029,Link004,Link005,Link007,Link008,Link009,Link010,Joint031,Joint034,Link011,Link013,Link012,+96 more]
  Origin = -> Origin
  Type = Assembly

RESOLVED EXTERNAL PARTS (link-assembly join: the EXTERNAL_REF files above that resolve inside this repo's crawl, each included once):
---- part Body/Body.FCStd = doc fcstd_7d97827781b7 (90630 chars; too large to inline — full recipe in that document) ----
---- part Imports/V-Groove.FCStd = doc fcstd_c98088faf659 ----
FCSTD DOCUMENT  (FreeCAD 1.1R42987 (Git))
Label: V-Groove
License: All rights reserved
LicenseURL: https://en.wikipedia.org/wiki/All_rights_reserved
objects: Sketcher::SketchObject×5, PartDesign::Pad×4, Part::Feature×3, App::Point×2, App::Part×1, PartDesign::SubShapeBinder×1, Part::DatumPlane×1, PartDesign::Pocket×1, PartDesign::Mirrored×1, PartDesign::Body×1
note: 32 computed .brp shape members not serialized (recipe doc carries the construction recipe); baked Part::Feature solids carry a one-line shape summary decoded from their .brp
EXTERNAL_REF file=../Variables.FCStd obj=Spreadsheet

FEATURE [Part::Feature] Part__Feature  label="1609-0613-0004"
  shape: bbox 9.277 x 0.3004 x 9.277 mm, 8 faces (baked)
FEATURE [Part::Feature] Part__Feature001  label="1609-0613-0005"
  shape: bbox 9.277 x 0.3004 x 9.277 mm, 8 faces (baked)
FEATURE [Part::Feature] Part__Feature002  label="1609-0613-0006"
  shape: bbox 13 x 6 x 13 mm, 66 faces (baked)
FEATURE [App::Part] _609_0613_0004  label="1609-0613-0007"
  Group = -> [Part__Feature,Part__Feature001,Part__Feature002]
  Origin = -> Origin
FEATURE [App::Point] Origin001
  Role = Origin
FEATURE [App::Point] Origin003
  Role = Origin
FEATURE [PartDesign::SubShapeBinder] Binder
  BindCopyOnChange = 0
  BindMode = 0
  ClaimChildren = false
  Context = -> Body [Binder.]
  Fuse = false
  MakeFace = true
  OffsetFill = false
  OffsetIntersection = false
  OffsetJoinType = 0
  OffsetOpenResult = false
  PartialLoad = false
  Refine = true
  Relative = true
  Support = -> [_609_0613_0004]
  _Version = 2
FEATURE [Sketcher::SketchObject] Sketch
  ArcFitTolerance = 1e-06
  AttachmentOffset = pos=(0,0,0.25) rot=(0,0,1;0rad)
  AttachmentSupport = -> [Binder]
  ExternalTypes = [0]
  FullyConstrained = true
  MakeInternals = false
  MapMode = 5
  Placement = pos=(0,-0.25,1e-16) rot=(1,0,0;1.5708rad)
  expr: Constraints[1] = Variables#Spreadsheet.M4ThroughBoreDiam
  sketch-geometry (2):
    g0: Circle CenterX=0 CenterY=0 CenterZ=0 NormalX=0 NormalY=0 NormalZ=1 AngleXU=0 Radius=2.175
    g1: Circle CenterX=0 CenterY=0 CenterZ=0 NormalX=0 NormalY=0 NormalZ=1 AngleXU=0 Radius=2.75
  constraints (4):
    c: Coincident(g0,g-1)
    c: Diameter(g0) = 4.35
    c: Coincident(g1,g0)
    c: Diameter(g1) = 5.5
FEATURE [PartDesign::Pad] Pad
  Direction = (0,-1,2e-16)
  Length = 1
  Length2 = 10
  Profile = -> Sketch
  ReferenceAxis = -> Sketch [N_Axis]
  Refine = true
  Suppressed = false
  Type = 0
FEATURE [Sketcher::SketchObject] Sketch001
  ArcFitTolerance = 1e-06
  AttachmentSupport = -> [Pad]
  ExternalGeometry = -> [Pad]
  ExternalTypes = [0]
  FullyConstrained = true
  MakeInternals = false
  MapMode = 5
  Placement = pos=(0,-1.25,3e-16) rot=(1,0,0;1.5708rad)
  sketch-geometry (4):
    g0: ArcOfCircle CenterX=0 CenterY=-4.3033e-12 CenterZ=0 NormalX=0 NormalY=0 NormalZ=1 AngleXU=0 Radius=4 StartAngle=3.14159 EndAngle=6.28319
    g1: LineSegment StartX=4 StartY=-6.67326e-11 StartZ=0 EndX=4 EndY=8 EndZ=0
    g2: LineSegment StartX=4 StartY=8 StartZ=0 EndX=-4 EndY=8 EndZ=0
    g3: LineSegment StartX=-4 StartY=8 StartZ=0 EndX=-4 EndY=-7.6463e-12 EndZ=0
  constraints (10):
    c: Coincident(g0,g-1)
    c: Vertical(g1)
    c: Coincident(g2,g1)
    c: Horizontal(g2)
    c: Coincident(g3,g2)
    c: Vertical(g3)
    c: DistanceY(g1,g1) = 8
    c: Diameter(g0) = 8
    c: Tangent(g1,g0) = -1.5708
    c: Tangent(g3,g0) = -1.5708
FEATURE [PartDesign::Pad] Pad001
  BaseFeature = -> Pad
  Direction = (0,-1,2e-16)
  Length = 2
  Length2 = 10
  Profile = -> Sketch001
  ReferenceAxis = -> Sketch001 [N_Axis]
  Refine = true
  Suppressed = false
  Type = 0
FEATURE [Sketcher::SketchObject] Sketch002
  ArcFitTolerance = 1e-06
  AttachmentSupport = -> [Pad001]
  ExternalGeometry = -> [Pad001]
  ExternalTypes = [0]
  FullyConstrained = true
  MakeInternals = false
  MapMode = 5
  Placement = pos=(0,-3.25,0) rot=(1,0,0;1.5708rad)
  sketch-geometry (3):
    g0: LineSegment StartX=-4 StartY=8 StartZ=0 EndX=-4 EndY=11 EndZ=0
    g1: LineSegment StartX=-4 StartY=11 StartZ=0 EndX=4 EndY=11 EndZ=0
    g2: LineSegment StartX=4 StartY=11 StartZ=0 EndX=4 EndY=8 EndZ=0
  constraints (8):
    c: Coincident(g-3,g0)
    c: Vertical(g0)
    c: Coincident(g0,g1)
    c: Horizontal(g1)
    c: Coincident(g1,g2)
    c: Coincident(g2,g-3)
    c: Vertical(g2)
    c: DistanceY(g2,g2) = 3
FEATURE [Part::DatumPlane] Plane
  AttachmentSupport = -> [Binder]
  MapMode = 11
  Placement = pos=(0,3,0) rot=(0,0.707107,0.707107;3.14159rad)
FEATURE [PartDesign::Pad] Pad002
  BaseFeature = -> Pad001
  Direction = (0,-1,2e-16)
  Length = 10
  Length2 = 10
  Profile = -> Sketch002
  ReferenceAxis = -> Sketch002 [N_Axis]
  Refine = true
  Suppressed = false
  Type = 3
  UpToFace = -> Plane
FEATURE [Sketcher::SketchObject] Sketch003
  ArcFitTolerance = 1e-06
  AttachmentSupport = -> [Pad002]
  ExternalGeometry = -> [Pad002]
  ExternalTypes = [0,0]
  FullyConstrained = true
  MakeInternals = false
  MapMode = 5
  Placement = pos=(-4,0,0) rot=(0.57735,-0.57735,-0.57735;2.0944rad)
  sketch-geometry (3):
    g0: LineSegment StartX=0.25 StartY=8 StartZ=0 EndX=1.25 EndY=8 EndZ=0
    g1: LineSegment StartX=1.25 StartY=8 StartZ=0 EndX=1.25 EndY=7 EndZ=0
    g2: ArcOfCircle CenterX=0.25 CenterY=7 CenterZ=0 NormalX=0 NormalY=0 NormalZ=1 AngleXU=0 Radius=1 StartAngle=-4.805e-13 EndAngle=1.5708
  constraints (7):
    c: PointOnObject(g0,g-3)
    c: Coincident(g0,g-4)
    c: Coincident(g0,g1)
    c: PointOnObject(g1,g-4)
    c: Tangent(g2,g0) = 1.5708
    c: Tangent(g2,g1) = 1.5708
    c: Radius(g2) = 1
FEATURE [PartDesign::Pad] Pad003
  BaseFeature = -> Pad002
  Direction = (-1,0,0)
  Length = 10
  Length2 = 10
  Profile = -> Sketch003
  ReferenceAxis = -> Sketch003 [N_Axis]
  Refine = true
  Suppressed = false
  Type = 3
  UpToFace = -> Pad002 [Face10]
FEATURE [Sketcher::SketchObject] Sketch004
  ArcFitTolerance = 1e-06
  AttachmentSupport = -> [Pad003]
  ExternalGeometry = -> [Pad003]
  ExternalTypes = [0,0,0]
  FullyConstrained = true
  MakeInternals = false
  MapMode = 5
  Placement = pos=(-4,0,0) rot=(0.57735,-0.57735,-0.57735;2.0944rad)
  sketch-geometry (3):
    g0: LineSegment StartX=2.25 StartY=11 StartZ=0 EndX=3.25 EndY=11 EndZ=0
    g1: LineSegment StartX=3.25 StartY=11 StartZ=0 EndX=3.25 EndY=10 EndZ=0
    g2: ArcOfCircle CenterX=2.25 CenterY=10 CenterZ=0 NormalX=0 NormalY=0 NormalZ=1 AngleXU=0 Radius=1 StartAngle=-3.624e-13 EndAngle=1.5708
  constraints (7):
    c: PointOnObject(g0,g-3)
    c: Coincident(g0,g-4)
    c: Coincident(g0,g1)
    c: PointOnObject(g1,g-4)
    c: Tangent(g2,g0) = 1.5708
    c: Tangent(g2,g1) = 1.5708
    c: Equal(g-5,g2)
FEATURE [PartDesign::Pocket] Pocket
  BaseFeature = -> Pad003
  Direction = (1,0,0)
  Length = 0
  Length2 = 5
  Profile = -> Sketch004
  ReferenceAxis = -> Sketch004 [N_Axis]
  Refine = true
  Suppressed = false
  Type = 3
  UpToFace = -> Pad003 [Face11]
FEATURE [PartDesign::Mirrored] Mirrored
  BaseFeature = -> Pocket
  MirrorPlane = -> Pad002 [Face7]
  Refine = true
  Suppressed = false
  TransformMode = 1
FEATURE [PartDesign::Body] Body  label="StringGuard"
  AllowCompound = true
  Group = -> [Binder,Sketch,Pad,Sketch001,Pad001,Sketch002,Plane,Pad002,Sketch003,Pad003,Sketch004,Pocket,Mirrored]
  Origin = -> Origin002
  Tip = -> Mirrored
---- part Spool/Spool.FCStd = doc fcstd_dbaecbb72555 ----
FCSTD DOCUMENT  (FreeCAD 1.1R42863 (Git))
Label: Spool
License: All rights reserved
LicenseURL: https://en.wikipedia.org/wiki/All_rights_reserved
objects: Sketcher::SketchObject×7, PartDesign::Pad×5, App::Point×2, PartDesign::Pocket×2, PartDesign::Chamfer×2, PartDesign::Body×2, Part::DatumPlane×1, PartDesign::PolarPattern×1, PartDesign::SubShapeBinder×1, PartDesign::Fillet×1
note: 49 computed .brp shape members not serialized (recipe doc carries the construction recipe); baked Part::Feature solids carry a one-line shape summary decoded from their .brp
EXTERNAL_REF file=../Variables.FCStd obj=Spreadsheet

FEATURE [App::Point] Origin001
  Role = Origin
FEATURE [Sketcher::SketchObject] Sketch
  ArcFitTolerance = 1e-06
  AttachmentSupport = -> [XY_Plane]
  ExternalTypes = [0]
  FullyConstrained = true
  MakeInternals = false
  MapMode = 5
  expr: Constraints[13] = Variables#Spreadsheet.SpoolInnerDiam
  expr: Constraints[7] = Variables#Spreadsheet.M4TapDiam
  sketch-geometry (7):
    g0: Circle CenterX=-2.798e-13 CenterY=0 CenterZ=0 NormalX=0 NormalY=0 NormalZ=1 AngleXU=0 Radius=17.5
    g1: LineSegment [constr] StartX=9 StartY=5 StartZ=0 EndX=9 EndY=-5 EndZ=0
    g2: GeomPoint [constr] X=9 Y=0 Z=0
    g3: Circle CenterX=9 CenterY=5 CenterZ=0 NormalX=0 NormalY=0 NormalZ=1 AngleXU=0 Radius=1.8
    g4: Circle CenterX=9 CenterY=-5 CenterZ=0 NormalX=0 NormalY=0 NormalZ=1 AngleXU=0 Radius=1.8
    g5: Circle CenterX=-2.798e-13 CenterY=0 CenterZ=0 NormalX=0 NormalY=0 NormalZ=1 AngleXU=0 Radius=3.125
    g6: Circle [constr] CenterX=-2.798e-13 CenterY=0 CenterZ=0 NormalX=0 NormalY=0 NormalZ=1 AngleXU=0 Radius=7.5
  constraints (15):
    c: Diameter(g0) = 35
    c: Coincident(g0,g-1)
    c: Distance(g1) = 10
    c: Vertical(g1)
    c: Symmetric(g1,g1,g2)
    c: PointOnObject(g2,g-1)
    c: Coincident(g3,g1)
    c: Diameter(g3) = 3.6
    c: Coincident(g4,g1)
    c: Equal(g4,g3)
    c: Diameter(g5) = 6.25
    c: Coincident(g5,g0)
    c: Coincident(g6,g0)
    c: Diameter(g6) = 15
    c: Distance(g2,g6) = 1.5
FEATURE [PartDesign::Pad] Pad
  Direction = (0,0,1)
  Length = 5
  Length2 = 10
  Profile = -> Sketch
  ReferenceAxis = -> Sketch [N_Axis]
  Refine = true
  Suppressed = false
  Type = 0
  expr: Length = Variables#Spreadsheet.SpoolWallThickness
FEATURE [Sketcher::SketchObject] Sketch001
  ArcFitTolerance = 1e-06
  AttachmentSupport = -> [Pad]
  ExternalGeometry = -> [Pad]
  ExternalTypes = [0]
  FullyConstrained = true
  MakeInternals = false
  MapMode = 5
  Placement = pos=(0,0,0) rot=(1,0,0;3.14159rad)
  expr: Constraints[0] = Variables#Spreadsheet.SpoolInnerDiam
  sketch-geometry (1):
    g0: Circle CenterX=0 CenterY=0 CenterZ=0 NormalX=0 NormalY=0 NormalZ=1 AngleXU=0 Radius=7.5
  constraints (2):
    c: Diameter(g0) = 15
    c: Coincident(g0,g-1)
FEATURE [PartDesign::Pad] Pad001
  BaseFeature = -> Pad
  Direction = (0,0,-1)
  Length = 35
  Length2 = 10
  Profile = -> Sketch001
  ReferenceAxis = -> Sketch001 [N_Axis]
  Refine = true
  Reversed = true
  Suppressed = false
  Type = 0
  expr: Length = Variables#Spreadsheet.SpoolThickness
FEATURE [Sketcher::SketchObject] Sketch002
  ArcFitTolerance = 1e-06
  AttachmentSupport = -> [Pad001]
  ExternalGeometry = -> [Pad001]
  ExternalTypes = [0,0]
  FullyConstrained = true
  MakeInternals = false
  MapMode = 5
  Placement = pos=(0,0,35) rot=(0,0,1;0rad)
FEATURE [PartDesign::Pad] Pad002
  BaseFeature = -> Pad001
  Direction = (0,0,1)
  Length = 5
  Length2 = 10
  Profile = -> Sketch002
  ReferenceAxis = -> Sketch002 [N_Axis]
  Refine = true
  Reversed = true
  Suppressed = false
  Type = 0
  expr: Length = Variables#Spreadsheet.SpoolWallThickness
FEATURE [Part::DatumPlane] DatumPlane
  AttachmentSupport = -> [Pad002]
  MapMode = 45
  Placement = pos=(-9e-16,0,17.5) rot=(0,0,1;0rad)
FEATURE [Sketcher::SketchObject] Sketch003
  ArcFitTolerance = 1e-06
  AttachmentSupport = -> [DatumPlane]
  ExternalGeometry = -> [Pad002]
  ExternalTypes = [0,0]
  FullyConstrained = true
  MakeInternals = false
  MapMode = 5
  Placement = pos=(-9e-16,0,17.5) rot=(0,0,1;0rad)
FEATURE [PartDesign::Pad] Pad003
  BaseFeature = -> Pad002
  Direction = (0,0,1)
  Length = 5
  Length2 = 10
  Midplane = true
  Profile = -> Sketch003
  ReferenceAxis = -> Sketch003 [N_Axis]
  Refine = true
  Suppressed = false
  Type = 0
  expr: Length = Variables#Spreadsheet.SpoolWallThickness
FEATURE [Sketcher::SketchObject] Sketch004
  ArcFitTolerance = 1e-06
  AttachmentSupport = -> [Pad003]
  ExternalGeometry = -> [Pad003]
  ExternalTypes = [0,0]
  FullyConstrained = true
  MakeInternals = false
  MapMode = 5
  Placement = pos=(0,0,20) rot=(0,0,1;0rad)
  sketch-geometry (5):
    g0: LineSegment [constr] StartX=9.5 StartY=-3 StartZ=0 EndX=9.5 EndY=3 EndZ=0
    g1: Circle CenterX=9.5 CenterY=-3 CenterZ=0 NormalX=0 NormalY=0 NormalZ=1 AngleXU=0 Radius=1.75
    g2: Circle CenterX=9.5 CenterY=3 CenterZ=0 NormalX=0 NormalY=0 NormalZ=1 AngleXU=0 Radius=1.75
    g3: GeomPoint [constr] X=7.5 Y=0 Z=0
    g4: GeomPoint [constr] X=9.5 Y=0 Z=0
  constraints (11):
    c: Vertical(g0)
    c: DistanceY(g0,g0) = 6
    c: Diameter(g1) = 3.5
    c: Coincident(g1,g0)
    c: Coincident(g2,g0)
    c: Equal(g1,g2)
    c: PointOnObject(g3,g-3)
    c: Symmetric(g0,g0,g4)
    c: PointOnObject(g3,g-1)
    c: PointOnObject(g4,g-1)
    c: DistanceX(g3,g4) = 2
FEATURE [PartDesign::Pocket] Pocket
  BaseFeature = -> Pad003
  Direction = (0,0,-1)
  Length = 0
  Length2 = 5
  Profile = -> Sketch004
  ReferenceAxis = -> Sketch004 [N_Axis]
  Refine = true
  Suppressed = false
  Type = 3
  UpToFace = -> Pad003 [Face10]
FEATURE [PartDesign::PolarPattern] PolarPattern
  Angle = 360
  Axis = -> Sketch004 [N_Axis]
  BaseFeature = -> Pocket
  Mode = 0
  Occurrences = 4
  Offset = 120
  Originals = -> [Pocket]
  Refine = true
  Suppressed = false
  TransformMode = 0
FEATURE [PartDesign::Chamfer] Chamfer
  Angle = 45
  Base = -> PolarPattern [Edge19,Edge30]
  BaseFeature = -> PolarPattern
  ChamferType = 0
  FlipDirection = false
  Refine = true
  Size = 2
  Size2 = 1
  SupportTransform = false
  Suppressed = false
  UseAllEdges = false
  expr: Size = Variables#Spreadsheet.SpoolWallThickness / 2 - 0.5
FEATURE [PartDesign::Chamfer] Chamfer001
  Angle = 45
  Base = -> Chamfer [Edge35,Edge41]
  BaseFeature = -> Chamfer
  ChamferType = 0
  FlipDirection = false
  Refine = true
  Size = 4
  Size2 = 1
  SupportTransform = false
  Suppressed = false
  UseAllEdges = false
  expr: Size = Variables#Spreadsheet.SpoolWallThickness - 1
FEATURE [PartDesign::Body] Body  label="Spool"
  AllowCompound = true
  Group = -> [Sketch,Pad,Sketch001,Pad001,Sketch002,Pad002,DatumPlane,Sketch003,Pad003,Sketch004,Pocket,PolarPattern,Chamfer,Chamfer001]
  Origin = -> Origin
  Tip = -> Chamfer001
FEATURE [App::Point] Origin003
  Role = Origin
FEATURE [PartDesign::SubShapeBinder] Binder
  BindCopyOnChange = 0
  BindMode = 0
  ClaimChildren = false
  Context = -> Body001 [Binder.]
  Fuse = false
  MakeFace = true
  OffsetFill = false
  OffsetIntersection = false
  OffsetJoinType = 0
  OffsetOpenResult = false
  PartialLoad = false
  Refine = true
  Relative = true
  Support = -> [Body]
  _Version = 2
FEATURE [Sketcher::SketchObject] Sketch005
  ArcFitTolerance = 1e-06
  AttachmentSupport = -> [Binder]
  ExternalGeometry = -> [Binder]
  ExternalTypes = [0,0,0]
  FullyConstrained = false
  MakeInternals = false
  MapMode = 5
  Placement = pos=(0,0,0) rot=(1,0,0;3.14159rad)
  expr: Constraints[34] = Variables#Spreadsheet.M4ThroughBoreDiam
  sketch-geometry (16):
    g0: ArcOfCircle CenterX=9 CenterY=5 CenterZ=0 NormalX=0 NormalY=0 NormalZ=1 AngleXU=0 Radius=4 StartAngle=-9e-16 EndAngle=1.90109
    g1: ArcOfCircle CenterX=9 CenterY=-5 CenterZ=0 NormalX=0 NormalY=0 NormalZ=1 AngleXU=0 Radius=4 StartAngle=4.38209 EndAngle=6.28319
    g2: LineSegment StartX=13 StartY=-5 StartZ=0 EndX=13 EndY=5 EndZ=0
    g3: LineSegment StartX=-11.5 StartY=7 StartZ=0 EndX=2.5 EndY=7 EndZ=0
    g4: LineSegment StartX=2.5 StartY=7 StartZ=0 EndX=7.7027 EndY=8.78378 EndZ=0
    g5: LineSegment StartX=-11.5 StartY=-7 StartZ=0 EndX=2.5 EndY=-7 EndZ=0
    g6: LineSegment StartX=2.5 StartY=-7 StartZ=0 EndX=7.7027 EndY=-8.78378 EndZ=0
    g7: GeomPoint X=0.731343 Y=-5.50967 Z=0
    g8: LineSegment StartX=-11.5 StartY=-7 StartZ=0 EndX=-11.5 EndY=-1.5 EndZ=0
    g9: ArcOfCircle CenterX=0 CenterY=0 CenterZ=0 NormalX=0 NormalY=0 NormalZ=1 AngleXU=0 Radius=3.075 StartAngle=3.65117 EndAngle=8.9152
    g10: LineSegment StartX=-11.5 StartY=7 StartZ=0 EndX=-11.5 EndY=1.5 EndZ=0
    g11: LineSegment StartX=-11.5 StartY=1.5 StartZ=0 EndX=-2.68433 EndY=1.5 EndZ=0
    g12: LineSegment StartX=-11.5 StartY=-1.5 StartZ=0 EndX=-2.68433 EndY=-1.5 EndZ=0
    g13: GeomPoint X=-11.5 Y=0 Z=0
    g14: Circle CenterX=9 CenterY=5 CenterZ=0 NormalX=0 NormalY=0 NormalZ=1 AngleXU=0 Radius=2.175
    g15: Circle CenterX=9 CenterY=-5 CenterZ=0 NormalX=0 NormalY=0 NormalZ=1 AngleXU=0 Radius=2.175
  constraints (37):
    c: Coincident(g0,g-3)
    c: Coincident(g1,g-4)
    c: Tangent(g2,g1) = -1.5708
    c: Tangent(g2,g0) = -1.5708
    c: Vertical(g2)
    c: Horizontal(g3)
    c: Coincident(g4,g3)
    c: Horizontal(g5)
    c: Coincident(g6,g5)
    c: Tangent(g6,g1) = -1.5708
    c: Tangent(g4,g0) = 1.5708
    c: Vertical(g3,g5)
    c: Vertical(g5,g3)
    c: Equal(g4,g6)
    c: DistanceX(g5,g5) = 14
    c: Distance(g5,g-2) = 2.5
    c: Coincident(g8,g5)
    c: Vertical(g8)
    c: Coincident(g9,g-1)
    c: Horizontal(g9,g8)
    c: Coincident(g10,g3)
    c: Vertical(g10)
    c: Coincident(g11,g10)
    c: Horizontal(g11)
    c: Coincident(g12,g8)
    c: Coincident(g12,g9)
    c: PointOnObject(g13,g-1)
    c: Symmetric(g10,g8,g13)
    c: Distance(g11,g12) = 3
    c: Distance(g3,g5) = 14
    c: Radius(g0) = 4
    c: Coincident(g9,g11)
    c: Radius(g9) = 3.075
    c: Coincident(g14,g0)
    c: Diameter(g14) = 4.35
    c: Coincident(g15,g1)
    c: Equal(g14,g15)
FEATURE [PartDesign::Pad] Pad004
  Direction = (0,0,-1)
  Length = 9
  Length2 = 10
  Profile = -> Sketch005
  ReferenceAxis = -> Sketch005 [N_Axis]
  Refine = true
  Suppressed = false
  Type = 0
FEATURE [Sketcher::SketchObject] Sketch006
  ArcFitTolerance = 1e-06
  AttachmentSupport = -> [Pad004]
  ExternalGeometry = -> [Pad004]
  ExternalTypes = [0]
  FullyConstrained = true
  MakeInternals = false
  MapMode = 5
  Placement = pos=(0,7,0) rot=(0,0.707107,0.707107;3.14159rad)
  expr: Constraints[1] = Variables#Spreadsheet.M4ThroughBoreDiam
  sketch-geometry (2):
    g0: GeomPoint [constr] X=11.5 Y=-4.5 Z=0
    g1: Circle CenterX=7.5 CenterY=-4.5 CenterZ=0 NormalX=0 NormalY=0 NormalZ=1 AngleXU=0 Radius=2.175
  constraints (4):
    c: Symmetric(g-3,g-3,g0)
    c: Diameter(g1) = 4.35
    c: Horizontal(g1,g0)
    c: DistanceX(g1,g0) = 4
FEATURE [PartDesign::Pocket] Pocket001
  BaseFeature = -> Pad004
  Direction = (0,-1,2e-16)
  Length = 0
  Length2 = 5
  Profile = -> Sketch006
  ReferenceAxis = -> Sketch006 [N_Axis]
  Refine = true
  Suppressed = false
  Type = 3
  UpToFace = -> Pad004 [Face7]
FEATURE [PartDesign::Fillet] Fillet
  Base = -> Pocket001 [Edge41,Edge43,Edge6,Edge1]
  BaseFeature = -> Pocket001
  Radius = 0.75
  Refine = true
  SupportTransform = false
  Suppressed = false
  UseAllEdges = false
FEATURE [PartDesign::Body] Body001  label="Spool CHub"
  AllowCompound = true
  Group = -> [Binder,Sketch005,Pad004,Sketch006,Pocket001,Fillet]
  Origin = -> Origin002
  Tip = -> Fillet
---- part Variables.FCStd = doc fcstd_5c9c6902009b ----
FCSTD DOCUMENT  (FreeCAD 1.1R40077 (Git))
Label: Variables
License: All rights reserved
LicenseURL: https://en.wikipedia.org/wiki/All_rights_reserved
objects: Spreadsheet::Sheet×1

FEATURE [Spreadsheet::Sheet] Spreadsheet  label="Variables"
  cells = A1='M4 Through OD; B1='M3 Through OD; C1='M4 Tap Diameter; D1='Washer grab diameter; A2(M4ThroughBoreDiam)=4.35; B2(M3ThroughBoreDiam)=3.5; C2(M4TapDiam)=3.6; D2(WasherGrabDiam)=30.5; A5='Wheel Base Size; B5='Slides Mount Offset; C5='Claw Height; D5='Passive Claw Mount X; E5='Passive Claw Mount Y; F5='Wheel ClampToShaft Dist; G5='Wheel Diam; H5='Support Slider Mount Line Dist; I5='Slider Pole Diam; J5='Slider Tolerance; K5='Passive Claw Mount Offset; L5='Clamp Z Offset; M5='SlidesMountX; N5='SlidesMountY; A6(WheelBaseSize)=100; B6(SlidesMountOffset)=55; C6(ClawHeight)==1.6 * 5 + 3; D6(PassiveClawMountX)=12; E6(PassiveClawMountY)=6; F6(WheelClampToShaftDist)=1.5; G6(WheelDiam)==55 mm; H6(SupportSliderMountLineDist)=20; I6(SliderPoleDiam)=10; J6(SliderTolerance)==0 mm; K6(PassiveClawMountOffset)=25; L6(ClampZOffset)=1; M6(SlidesMountX)=45; N6(SlidesMountY)=20; A8='Spool Thickness; B8='Spool Wall Thickness; C8='Spool Inner Diam; A9(SpoolThickness)=35; B9(SpoolWallThickness)=5; C9(SpoolInnerDiam)=15
---- part Wheel/Wheel.FCStd = doc fcstd_3e58f8c0e0f4 ----
FCSTD DOCUMENT  (FreeCAD 1.1R42863 (Git))
Label: Wheel
License: All rights reserved
LicenseURL: https://en.wikipedia.org/wiki/All_rights_reserved
objects: Sketcher::SketchObject×8, PartDesign::Pocket×4, App::Point×3, PartDesign::Pad×3, Part::DatumPlane×2, PartDesign::Body×2, PartDesign::SubShapeBinder×1, Part::LocalCoordinateSystem×1, PartDesign::Groove×1, PartDesign::Mirrored×1
note: 45 computed .brp shape members not serialized (recipe doc carries the construction recipe); baked Part::Feature solids carry a one-line shape summary decoded from their .brp
EXTERNAL_REF file=../Variables.FCStd obj=Spreadsheet

FEATURE [App::Point] Origin001
  Role = Origin
FEATURE [Sketcher::SketchObject] Sketch
  ArcFitTolerance = 1e-06
  AttachmentSupport = -> [XY_Plane]
  ExternalTypes = [0]
  FullyConstrained = true
  MakeInternals = false
  MapMode = 5
  expr: Constraints[0] = Variables#Spreadsheet.WheelDiam
  sketch-geometry (2):
    g0: Circle CenterX=0 CenterY=0 CenterZ=0 NormalX=0 NormalY=0 NormalZ=1 AngleXU=0 Radius=27.5
    g1: Circle CenterX=0 CenterY=0 CenterZ=0 NormalX=0 NormalY=0 NormalZ=1 AngleXU=0 Radius=3.025
  constraints (4):
    c: Diameter(g0) = 55
    c: Coincident(g0,g-1)
    c: Coincident(g1,g0)
    c: Diameter(g1) = 6.05
FEATURE [PartDesign::Pad] Pad
  Direction = (0,0,1)
  Length = 12.5
  Length2 = 10
  Profile = -> Sketch
  ReferenceAxis = -> Sketch [N_Axis]
  Refine = true
  Suppressed = false
  Type = 0
FEATURE [Sketcher::SketchObject] Sketch001
  ArcFitTolerance = 1e-06
  AttachmentSupport = -> [Pad]
  ExternalGeometry = -> [Pad]
  ExternalTypes = [0]
  FullyConstrained = false
  MakeInternals = false
  MapMode = 5
  Placement = pos=(0,0,12.5) rot=(0,0,1;0rad)
  expr: Constraints[17] = Variables#Spreadsheet.M4ThroughBoreDiam
  expr: Constraints[3] = Variables#Spreadsheet.WheelClampToShaftDist / 2
  sketch-geometry (13):
    g0: LineSegment StartX=-2.93055 StartY=-0.75 StartZ=0 EndX=-14 EndY=-0.75 EndZ=0
    g1: LineSegment StartX=14 StartY=-0.75 StartZ=0 EndX=2.88425 EndY=-0.75 EndZ=0
    g2: ArcOfCircle CenterX=-0.0231521 CenterY=0.025307 CenterZ=0 NormalX=0 NormalY=0 NormalZ=1 AngleXU=0 Radius=3.009 StartAngle=3.4022 EndAngle=6.02258
    g3: LineSegment [constr] StartX=0 StartY=-13.75 StartZ=0 EndX=0 EndY=-16.75 EndZ=0
    g4: LineSegment StartX=4 StartY=-16.75 StartZ=0 EndX=4 EndY=-13.75 EndZ=0
    g5: LineSegment StartX=-4 StartY=-16.75 StartZ=0 EndX=-4 EndY=-13.75 EndZ=0
    g6: ArcOfCircle CenterX=0 CenterY=-16.75 CenterZ=0 NormalX=0 NormalY=0 NormalZ=1 AngleXU=0 Radius=4 StartAngle=3.14159 EndAngle=6.28319
    g7: Circle CenterX=0 CenterY=-16.75 CenterZ=0 NormalX=0 NormalY=0 NormalZ=1 AngleXU=0 Radius=2.175
    g8: LineSegment StartX=-4 StartY=-13.75 StartZ=0 EndX=-14 EndY=-13.75 EndZ=0
    g9: LineSegment StartX=-14 StartY=-13.75 StartZ=0 EndX=-14 EndY=-0.75 EndZ=0
    g10: LineSegment StartX=4 StartY=-13.75 StartZ=0 EndX=14 EndY=-13.75 EndZ=0
    g11: LineSegment StartX=14 StartY=-13.75 StartZ=0 EndX=14 EndY=-0.75 EndZ=0
    g12: GeomPoint X=0 Y=-0.75 Z=0
  constraints (34):
    c: PointOnObject(g0,g-3)
    c: Horizontal(g0)
    c: Horizontal(g1)
    c: Distance(g-1,g0) = 0.75
    c: Coincident(g2,g0)
    c: Coincident(g2,g1)
    c: Distance(g3) = 3
    c: PointOnObject(g3,g-2)
    c: Vertical(g3)
    c: Vertical(g4)
    c: Vertical(g5)
    c: Coincident(g6,g3)
    c: Tangent(g6,g4) = -1.5708
    c: Tangent(g6,g5) = 1.5708
    c: Radius(g6) = 4
    c: Horizontal(g1,g0)
    c: Coincident(g7,g3)
    c: Diameter(g7) = 4.35
    c: Coincident(g8,g5)
    c: Horizontal(g8)
    c: Coincident(g9,g8)
    c: Coincident(g9,g0)
    c: Vertical(g9)
    c: Coincident(g10,g4)
    c: Horizontal(g10)
    c: Coincident(g11,g10)
    c: Coincident(g11,g1)
    c: Vertical(g11)
    c: PointOnObject(g3,g10)
    c: Horizontal(g4,g5)
    c: Distance(g1,g10) = 13
    c: Symmetric(g0,g1,g12)
    c: PointOnObject(g12,g-2)
    c: Distance(g11,g9) = 28
FEATURE [PartDesign::Pad] Pad001
  BaseFeature = -> Pad
  Direction = (0,0,1)
  Length = 9
  Length2 = 10
  Profile = -> Sketch001
  ReferenceAxis = -> Sketch001 [N_Axis]
  Refine = true
  Suppressed = false
  Type = 0
FEATURE [Sketcher::SketchObject] Sketch002
  ArcFitTolerance = 1e-06
  AttachmentSupport = -> [Pad001]
  ExternalGeometry = -> [Pad001]
  ExternalTypes = [0,0,0,0]
  FullyConstrained = true
  MakeInternals = false
  MapMode = 5
  Placement = pos=(0,-0.75,0) rot=(0,0.707107,0.707107;3.14159rad)
  expr: Constraints[2] = 4.2
  sketch-geometry (6):
    g0: GeomPoint [constr] X=-8.44212 Y=21.5 Z=0
    g1: GeomPoint [constr] X=-2.88425 Y=17 Z=0
    g2: Circle CenterX=-8.44212 CenterY=17 CenterZ=0 NormalX=0 NormalY=0 NormalZ=1 AngleXU=0 Radius=2.1
    g3: GeomPoint X=8.46528 Y=21.5 Z=0
    g4: Circle CenterX=8.46528 CenterY=17 CenterZ=0 NormalX=0 NormalY=0 NormalZ=1 AngleXU=0 Radius=2.1
    g5: GeomPoint X=2.93055 Y=17 Z=0
  constraints (10):
    c: Vertical(g2,g0)
    c: Horizontal(g2,g1)
    c: Diameter(g2) = 4.2
    c: Equal(g4,g2)
    c: Horizontal(g2,g4)
    c: Vertical(g4,g3)
    c: Symmetric(g-3,g-3,g5)
    c: Symmetric(g-4,g-4,g1)
    c: Symmetric(g-5,g-5,g0)
    c: Symmetric(g-6,g-6,g3)
FEATURE [PartDesign::Pocket] Pocket
  BaseFeature = -> Pad001
  Direction = (0,-1,2e-16)
  Length = 5
  Length2 = 5
  Profile = -> Sketch002
  ReferenceAxis = -> Sketch002 [N_Axis]
  Refine = true
  Suppressed = false
  Type = 1
FEATURE [App::Point] Origin003
  Role = Origin
FEATURE [PartDesign::SubShapeBinder] Binder
  BindCopyOnChange = 0
  BindMode = 0
  ClaimChildren = false
  Context = -> Body001 [Binder.]
  Fuse = false
  MakeFace = true
  OffsetFill = false
  OffsetIntersection = false
  OffsetJoinType = 0
  OffsetOpenResult = false
  PartialLoad = false
  Refine = true
  Relative = true
  Support = -> [Body]
  _Version = 2
FEATURE [Sketcher::SketchObject] Sketch003
  ArcFitTolerance = 1e-06
  AttachmentOffset = pos=(0,0,-1) rot=(0,0,1;0rad)
  AttachmentSupport = -> [Binder]
  ExternalGeometry = -> [Binder]
  ExternalTypes = [0,0,0]
  FullyConstrained = true
  MakeInternals = false
  MapMode = 5
  Placement = pos=(0,0,20.5) rot=(0,0,1;0rad)
  expr: .AttachmentOffset.Base.z = -Variables#Spreadsheet.ClampZOffset
  expr: Constraints[26] = Variables#Spreadsheet.WheelClampToShaftDist
  sketch-geometry (14):
    g0: LineSegment StartX=14 StartY=0.75 StartZ=0 EndX=4.20573 EndY=0.75 EndZ=0
    g1: LineSegment StartX=-4.20573 StartY=0.75 StartZ=0 EndX=-14 EndY=0.75 EndZ=0
    g2: ArcOfCircle CenterX=7.012e-13 CenterY=2.9e-15 CenterZ=0 NormalX=0 NormalY=0 NormalZ=1 AngleXU=0 Radius=3.025 StartAngle=0.579091 EndAngle=2.5625
    g3: LineSegment StartX=14 StartY=0.75 StartZ=0 EndX=14 EndY=6.75 EndZ=0
    g4: LineSegment StartX=12 StartY=8.75 StartZ=0 EndX=-12 EndY=8.75 EndZ=0
    g5: LineSegment StartX=-14 StartY=6.75 StartZ=0 EndX=-14 EndY=0.75 EndZ=0
    g6: LineSegment [constr] StartX=14 StartY=-0.75 StartZ=0 EndX=14 EndY=0.75 EndZ=0
    g7: GeomPoint [constr] X=14 Y=4.9e-15 Z=0
    g8: ArcOfCircle CenterX=12 CenterY=6.75 CenterZ=0 NormalX=0 NormalY=0 NormalZ=1 AngleXU=0 Radius=2 StartAngle=-2.7e-15 EndAngle=1.5708
    g9: GeomPoint [constr] X=14 Y=8.75 Z=0
    g10: ArcOfCircle CenterX=-12 CenterY=6.75 CenterZ=0 NormalX=0 NormalY=0 NormalZ=1 AngleXU=0 Radius=2 StartAngle=1.5708 EndAngle=3.14159
    g11: GeomPoint [constr] X=-14 Y=8.75 Z=0
    g12: ArcOfCircle CenterX=-4.20573 CenterY=2.75 CenterZ=0 NormalX=0 NormalY=0 NormalZ=1 AngleXU=0 Radius=2 StartAngle=4.71239 EndAngle=5.70409
    g13: ArcOfCircle CenterX=4.20573 CenterY=2.75 CenterZ=0 NormalX=0 NormalY=0 NormalZ=1 AngleXU=0 Radius=2 StartAngle=3.72068 EndAngle=4.71239
  constraints (34):
    c: Horizontal(g0)
    c: Horizontal(g1)
    c: Coincident(g3,g0)
    c: Vertical(g3)
    c: Horizontal(g4)
    c: Coincident(g5,g1)
    c: Vertical(g5)
    c: Equal(g0,g1)
    c: Coincident(g2,g-1)
    c: Coincident(g6,g0)
    c: Symmetric(g6,g6,g7)
    c: PointOnObject(g7,g-1)
    c: PointOnObject(g9,g3)
    c: PointOnObject(g9,g4)
    c: Tangent(g3,g8) = -1.5708
    c: Tangent(g4,g8) = -1.5708
    c: PointOnObject(g11,g4)
    c: PointOnObject(g11,g5)
    c: Tangent(g4,g10) = -1.5708
    c: Tangent(g5,g10) = -1.5708
    c: Radius(g10) = 2
    c: Equal(g10,g8)
    c: Vertical(g6)
    c: Equal(g2,g-3)
    c: Distance(g0,g4) = 8
    c: Vertical(g1,g-5)
    c: Distance(g-5,g1) = 1.5
    c: Tangent(g2,g12) = 1.5708
    c: Tangent(g1,g12) = 1.5708
    c: Tangent(g2,g13) = 1.5708
    c: Tangent(g0,g13) = 1.5708
    c: Radius(g13) = 2
    c: Equal(g12,g13)
    c: PointOnObject(g0,g1)
FEATURE [App::Point] Origin004
  Role = Origin
FEATURE [Part::LocalCoordinateSystem] LCS
  AttacherType = Attacher::AttachEngine3D
  AttachmentSupport = -> [Pocket]
  MapMode = 11
  OriginFeatures = -> [X_Axis002,Y_Axis002,Z_Axis002,XY_Plane002,XZ_Plane002,YZ_Plane002,Origin004]
  Placement = pos=(-3.6e-15,0,12.5) rot=(0,0,1;1.5708rad)
FEATURE [Sketcher::SketchObject] Sketch005
  ArcFitTolerance = 1e-06
  AttachmentSupport = -> [XZ_Plane002]
  ExternalGeometry = -> [Pocket]
  ExternalTypes = [0]
  FullyConstrained = true
  MakeInternals = false
  MapMode = 5
  Placement = pos=(0,0,0) rot=(1,0,0;1.5708rad)
  sketch-geometry (3):
    g0: LineSegment StartX=-27.5 StartY=-1.54e-13 StartZ=0 EndX=-27.5 EndY=3 EndZ=0
    g1: LineSegment StartX=-27.5 StartY=-1.54e-13 StartZ=0 EndX=-24.5 EndY=4.454e-13 EndZ=0
    g2: ArcOfCircle CenterX=-24.5 CenterY=3 CenterZ=0 NormalX=0 NormalY=0 NormalZ=1 AngleXU=0 Radius=3 StartAngle=3.14159 EndAngle=4.71239
  constraints (7):
    c: Coincident(g0,g-3)
    c: Vertical(g0)
    c: Coincident(g1,g0)
    c: PointOnObject(g1,g-3)
    c: Tangent(g2,g0) = 1.5708
    c: Tangent(g2,g1) = -1.5708
    c: Radius(g2) = 3
FEATURE [PartDesign::Groove] Groove
  Angle = 360
  Angle2 = 60
  Axis = (0,2e-16,1)
  Base = (0,0,0)
  BaseFeature = -> Pocket
  Profile = -> Sketch005
  ReferenceAxis = -> Sketch005 [V_Axis]
  Refine = true
  Reversed = true
  Suppressed = false
  Type = 0
FEATURE [Part::DatumPlane] DatumPlane
  AttachmentSupport = -> [Pocket]
  MapMode = 45
  Placement = pos=(-1.07e-14,-5e-16,6.25) rot=(0,0,1;0rad)
FEATURE [PartDesign::Mirrored] Mirrored
  BaseFeature = -> Groove
  MirrorPlane = -> DatumPlane
  Originals = -> [Groove]
  Refine = true
  Suppressed = false
  TransformMode = 0
FEATURE [PartDesign::Pad] Pad002
  Direction = (0,0,1)
  Length = 10
  Length2 = 10
  Offset = -1
  Profile = -> Sketch003
  ReferenceAxis = -> Sketch003 [N_Axis]
  Refine = true
  Suppressed = false
  Type = 3
  UpToFace = -> Mirrored [Face5]
  expr: Offset = -Variables#Spreadsheet.ClampZOffset
FEATURE [Sketcher::SketchObject] Sketch004
  ArcFitTolerance = 1e-06
  AttachmentSupport = -> [Pad002]
  ExternalGeometry = -> [Binder]
  ExternalTypes = [0,0]
  FullyConstrained = true
  MakeInternals = false
  MapMode = 5
  Placement = pos=(0,8.75,0) rot=(0,0.707107,0.707107;3.14159rad)
FEATURE [PartDesign::Pocket] Pocket001
  BaseFeature = -> Pad002
  Direction = (0,-1,2e-16)
  Length = 0
  Length2 = 5
  Profile = -> Sketch004
  ReferenceAxis = -> Sketch004 [N_Axis]
  Refine = true
  Suppressed = false
  Type = 3
  UpToFace = -> Pad002 [Face5]
FEATURE [PartDesign::Body] Body001  label="Clamp"
  AllowCompound = true
  Group = -> [Binder,Sketch003,Pad002,Sketch004,Pocket001]
  Origin = -> Origin002
  Tip = -> Pocket001
FEATURE [Part::DatumPlane] DatumPlane001
  AttachmentOffset = pos=(0,0,0) rot=(0,1,0;1.5708rad)
  AttachmentSupport = -> [Mirrored]
  MapMode = 11
  Placement = pos=(-8.46528,-0.75,17) rot=(0,0,1;4.71239rad)
FEATURE [Sketcher::SketchObject] Sketch007
  ArcFitTolerance = 1e-06
  ExternalGeometry = -> [Mirrored]
  ExternalTypes = [0]
  FullyConstrained = true
  MakeInternals = false
  MapMode = 5
  Placement = pos=(0,0,21.5) rot=(0,0,1;0rad)
  expr: Constraints[1] = Variables#Spreadsheet.M4ThroughBoreDiam
  sketch-geometry (1):
    g0: Circle CenterX=0 CenterY=-7.75 CenterZ=0 NormalX=0 NormalY=0 NormalZ=1 AngleXU=0 Radius=2.175
  constraints (3):
    c: PointOnObject(g0,g-2)
    c: Diameter(g0) = 4.35
    c: DistanceY(g-3,g0) = 9
FEATURE [PartDesign::Pocket] Pocket002
  BaseFeature = -> Mirrored
  Direction = (0,0,-1)
  Length = 0
  Length2 = 5
  Profile = -> Sketch007
  ReferenceAxis = -> Sketch007 [N_Axis]
  Refine = true
  Suppressed = false
  Type = 3
  UpToFace = -> Mirrored [Face4]
FEATURE [Sketcher::SketchObject] Sketch008
  ArcFitTolerance = 1e-06
  AttachmentSupport = -> [Pocket002]
  ExternalGeometry = -> [Pocket002]
  ExternalTypes = [0]
  FullyConstrained = true
  MakeInternals = false
  MapMode = 5
  Placement = pos=(0,0,21.5) rot=(0,0,1;0rad)
FEATURE [PartDesign::Pocket] Pocket003
  BaseFeature = -> Pocket002
  Direction = (0,0,-1)
  Length = 0
  Length2 = 5
  Profile = -> Sketch008
  ReferenceAxis = -> Sketch008 [N_Axis]
  Refine = true
  Suppressed = false
  Type = 3
  UpToFace = -> Pocket002 [Face4]
FEATURE [PartDesign::Body] Body  label="Wheel"
  AllowCompound = true
  Group = -> [Sketch,Pad,Sketch001,Pad001,Sketch002,Pocket,LCS,Sketch005,DatumPlane,Groove,Mirrored,DatumPlane001,Sketch007,Pocket002,Sketch008,Pocket003]
  Origin = -> Origin
  Tip = -> Pocket003
